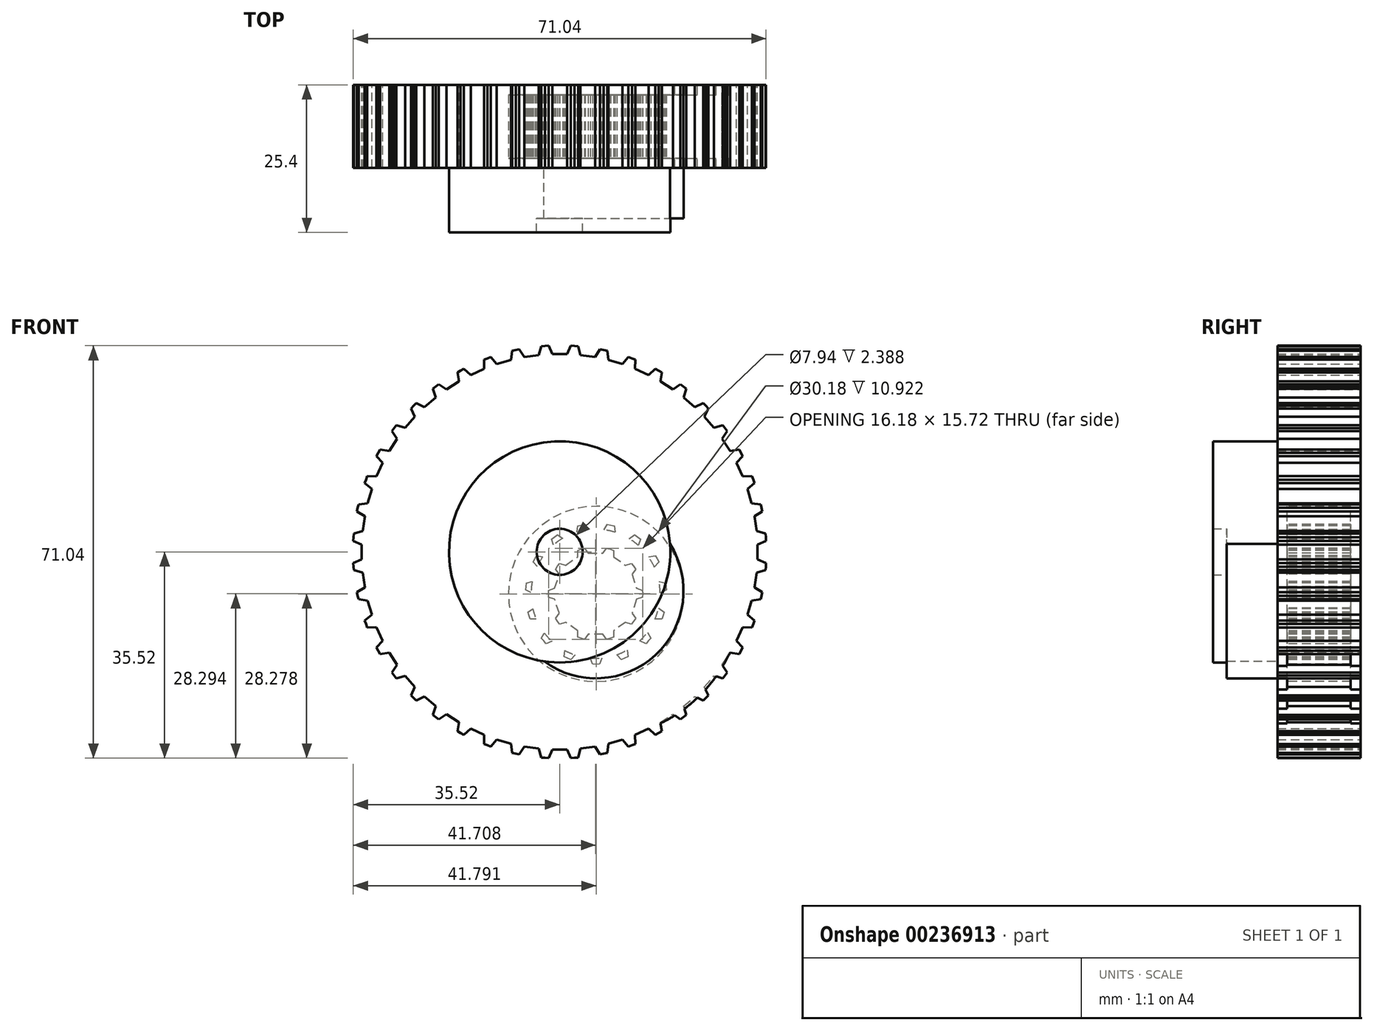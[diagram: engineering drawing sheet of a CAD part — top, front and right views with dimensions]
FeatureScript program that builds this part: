
annotation { "Feature Type Name" : "Feature", "Feature Type Description" : "" }
export const myFeature = defineFeature(function(context is Context, id is Id, definition is map)
    precondition{}
    {
        {
            var Q0;
            Q0=qCreatedBy(makeId("Front.planeOp"),FACE);
            var sketch = newSketch(context, id + "F0", { "sketchPlane" : qUnion([Q0])});
            skCircle(sketch, "E0", {"center": v(0, 0) * mm, "radius": 15.09 * mm});
            skCircle(sketch, "E1", {"center": v(0, 0) * mm, "radius": 22.64 * mm, "construction": true});
            skCircle(sketch, "E2", {"center": v(0, 0) * mm, "radius": 3.17 * mm});
            skCircle(sketch, "E3", {"center": v(0, 0) * mm, "radius": 25.4 * mm});
            skPoint(sketch, "E4", {"position": v(-2.54, 22.5) * mm});
            skPoint(sketch, "E5", {"position": v(2.54, 22.5) * mm});
            skPoint(sketch, "E6", {"position": v(-1.9, 22.56) * mm});
            skPoint(sketch, "E7", {"position": v(1.9, 22.56) * mm});
            skLineSegment(sketch, "E8", {"start": v(-2.54, 22.5) * mm, "end": v(-1.9, 22.56) * mm});
            skLineSegment(sketch, "E9", {"start": v(1.9, 22.56) * mm, "end": v(2.54, 22.5) * mm});
            skLineSegment(sketch, "E10", {"start": v(-1.9, 22.56) * mm, "end": v(-1.27, 21.24) * mm});
            skLineSegment(sketch, "E11", {"start": v(-1.27, 21.24) * mm, "end": v(1.27, 21.24) * mm});
            skLineSegment(sketch, "E12", {"start": v(1.27, 21.24) * mm, "end": v(1.9, 22.56) * mm});
            skLineSegment(sketch, "E13.1.0", {"start": v(-7.48, 21.37) * mm, "end": v(-6.88, 21.57) * mm});
            skLineSegment(sketch, "E13.1.1", {"start": v(-6.88, 21.57) * mm, "end": v(-5.96, 20.43) * mm});
            skLineSegment(sketch, "E13.1.2", {"start": v(-5.96, 20.43) * mm, "end": v(-3.49, 21) * mm});
            skLineSegment(sketch, "E13.1.3", {"start": v(-3.49, 21) * mm, "end": v(-3.16, 22.42) * mm});
            skLineSegment(sketch, "E13.1.4", {"start": v(-3.16, 22.42) * mm, "end": v(-2.53, 22.5) * mm});
            skLineSegment(sketch, "E13.2.0", {"start": v(-12.05, 19.17) * mm, "end": v(-11.5, 19.5) * mm});
            skLineSegment(sketch, "E13.2.1", {"start": v(-11.5, 19.5) * mm, "end": v(-10.36, 18.59) * mm});
            skLineSegment(sketch, "E13.2.2", {"start": v(-10.36, 18.59) * mm, "end": v(-8.07, 19.69) * mm});
            skLineSegment(sketch, "E13.2.3", {"start": v(-8.07, 19.69) * mm, "end": v(-8.07, 21.16) * mm});
            skLineSegment(sketch, "E13.2.4", {"start": v(-8.07, 21.16) * mm, "end": v(-7.47, 21.37) * mm});
            skLineSegment(sketch, "E13.3.0", {"start": v(-16.02, 16) * mm, "end": v(-15.56, 16.45) * mm});
            skLineSegment(sketch, "E13.3.1", {"start": v(-15.56, 16.45) * mm, "end": v(-14.24, 15.81) * mm});
            skLineSegment(sketch, "E13.3.2", {"start": v(-14.24, 15.81) * mm, "end": v(-12.25, 17.4) * mm});
            skLineSegment(sketch, "E13.3.3", {"start": v(-12.25, 17.4) * mm, "end": v(-12.58, 18.83) * mm});
            skLineSegment(sketch, "E13.3.4", {"start": v(-12.58, 18.83) * mm, "end": v(-12.04, 19.18) * mm});
            skLineSegment(sketch, "E13.4.0", {"start": v(-19.18, 12.04) * mm, "end": v(-18.83, 12.58) * mm});
            skLineSegment(sketch, "E13.4.1", {"start": v(-18.83, 12.58) * mm, "end": v(-17.4, 12.25) * mm});
            skLineSegment(sketch, "E13.4.2", {"start": v(-17.4, 12.25) * mm, "end": v(-15.81, 14.24) * mm});
            skLineSegment(sketch, "E13.4.3", {"start": v(-15.81, 14.24) * mm, "end": v(-16.45, 15.56) * mm});
            skLineSegment(sketch, "E13.4.4", {"start": v(-16.45, 15.56) * mm, "end": v(-16, 16.02) * mm});
            skLineSegment(sketch, "E13.5.0", {"start": v(-21.37, 7.47) * mm, "end": v(-21.16, 8.07) * mm});
            skLineSegment(sketch, "E13.5.1", {"start": v(-21.16, 8.07) * mm, "end": v(-19.69, 8.07) * mm});
            skLineSegment(sketch, "E13.5.2", {"start": v(-19.69, 8.07) * mm, "end": v(-18.59, 10.36) * mm});
            skLineSegment(sketch, "E13.5.3", {"start": v(-18.59, 10.36) * mm, "end": v(-19.5, 11.5) * mm});
            skLineSegment(sketch, "E13.5.4", {"start": v(-19.5, 11.5) * mm, "end": v(-19.17, 12.05) * mm});
            skLineSegment(sketch, "E13.6.0", {"start": v(-22.5, 2.53) * mm, "end": v(-22.42, 3.16) * mm});
            skLineSegment(sketch, "E13.6.1", {"start": v(-22.42, 3.16) * mm, "end": v(-21, 3.49) * mm});
            skLineSegment(sketch, "E13.6.2", {"start": v(-21, 3.49) * mm, "end": v(-20.43, 5.96) * mm});
            skLineSegment(sketch, "E13.6.3", {"start": v(-20.43, 5.96) * mm, "end": v(-21.57, 6.88) * mm});
            skLineSegment(sketch, "E13.6.4", {"start": v(-21.57, 6.88) * mm, "end": v(-21.37, 7.48) * mm});
            skLineSegment(sketch, "E13.7.0", {"start": v(-22.5, -2.54) * mm, "end": v(-22.56, -1.9) * mm});
            skLineSegment(sketch, "E13.7.1", {"start": v(-22.56, -1.9) * mm, "end": v(-21.24, -1.27) * mm});
            skLineSegment(sketch, "E13.7.2", {"start": v(-21.24, -1.27) * mm, "end": v(-21.24, 1.27) * mm});
            skLineSegment(sketch, "E13.7.3", {"start": v(-21.24, 1.27) * mm, "end": v(-22.56, 1.9) * mm});
            skLineSegment(sketch, "E13.7.4", {"start": v(-22.56, 1.9) * mm, "end": v(-22.5, 2.54) * mm});
            skLineSegment(sketch, "E13.8.0", {"start": v(-21.37, -7.48) * mm, "end": v(-21.57, -6.88) * mm});
            skLineSegment(sketch, "E13.8.1", {"start": v(-21.57, -6.88) * mm, "end": v(-20.43, -5.96) * mm});
            skLineSegment(sketch, "E13.8.2", {"start": v(-20.43, -5.96) * mm, "end": v(-21, -3.49) * mm});
            skLineSegment(sketch, "E13.8.3", {"start": v(-21, -3.49) * mm, "end": v(-22.42, -3.16) * mm});
            skLineSegment(sketch, "E13.8.4", {"start": v(-22.42, -3.16) * mm, "end": v(-22.5, -2.53) * mm});
            skLineSegment(sketch, "E13.9.0", {"start": v(-19.17, -12.05) * mm, "end": v(-19.5, -11.5) * mm});
            skLineSegment(sketch, "E13.9.1", {"start": v(-19.5, -11.5) * mm, "end": v(-18.59, -10.36) * mm});
            skLineSegment(sketch, "E13.9.2", {"start": v(-18.59, -10.36) * mm, "end": v(-19.69, -8.07) * mm});
            skLineSegment(sketch, "E13.9.3", {"start": v(-19.69, -8.07) * mm, "end": v(-21.16, -8.07) * mm});
            skLineSegment(sketch, "E13.9.4", {"start": v(-21.16, -8.07) * mm, "end": v(-21.37, -7.47) * mm});
            skLineSegment(sketch, "E13.10.0", {"start": v(-16, -16.02) * mm, "end": v(-16.45, -15.56) * mm});
            skLineSegment(sketch, "E13.10.1", {"start": v(-16.45, -15.56) * mm, "end": v(-15.81, -14.24) * mm});
            skLineSegment(sketch, "E13.10.2", {"start": v(-15.81, -14.24) * mm, "end": v(-17.4, -12.25) * mm});
            skLineSegment(sketch, "E13.10.3", {"start": v(-17.4, -12.25) * mm, "end": v(-18.83, -12.58) * mm});
            skLineSegment(sketch, "E13.10.4", {"start": v(-18.83, -12.58) * mm, "end": v(-19.18, -12.04) * mm});
            skLineSegment(sketch, "E13.11.0", {"start": v(-12.04, -19.18) * mm, "end": v(-12.58, -18.83) * mm});
            skLineSegment(sketch, "E13.11.1", {"start": v(-12.58, -18.83) * mm, "end": v(-12.25, -17.4) * mm});
            skLineSegment(sketch, "E13.11.2", {"start": v(-12.25, -17.4) * mm, "end": v(-14.24, -15.81) * mm});
            skLineSegment(sketch, "E13.11.3", {"start": v(-14.24, -15.81) * mm, "end": v(-15.56, -16.45) * mm});
            skLineSegment(sketch, "E13.11.4", {"start": v(-15.56, -16.45) * mm, "end": v(-16.02, -16) * mm});
            skLineSegment(sketch, "E13.12.0", {"start": v(-7.47, -21.37) * mm, "end": v(-8.07, -21.16) * mm});
            skLineSegment(sketch, "E13.12.1", {"start": v(-8.07, -21.16) * mm, "end": v(-8.07, -19.69) * mm});
            skLineSegment(sketch, "E13.12.2", {"start": v(-8.07, -19.69) * mm, "end": v(-10.36, -18.59) * mm});
            skLineSegment(sketch, "E13.12.3", {"start": v(-10.36, -18.59) * mm, "end": v(-11.5, -19.5) * mm});
            skLineSegment(sketch, "E13.12.4", {"start": v(-11.5, -19.5) * mm, "end": v(-12.05, -19.17) * mm});
            skLineSegment(sketch, "E13.13.0", {"start": v(-2.53, -22.5) * mm, "end": v(-3.16, -22.42) * mm});
            skLineSegment(sketch, "E13.13.1", {"start": v(-3.16, -22.42) * mm, "end": v(-3.49, -21) * mm});
            skLineSegment(sketch, "E13.13.2", {"start": v(-3.49, -21) * mm, "end": v(-5.96, -20.43) * mm});
            skLineSegment(sketch, "E13.13.3", {"start": v(-5.96, -20.43) * mm, "end": v(-6.88, -21.57) * mm});
            skLineSegment(sketch, "E13.13.4", {"start": v(-6.88, -21.57) * mm, "end": v(-7.48, -21.37) * mm});
            skLineSegment(sketch, "E13.14.0", {"start": v(2.54, -22.5) * mm, "end": v(1.9, -22.56) * mm});
            skLineSegment(sketch, "E13.14.1", {"start": v(1.9, -22.56) * mm, "end": v(1.27, -21.24) * mm});
            skLineSegment(sketch, "E13.14.2", {"start": v(1.27, -21.24) * mm, "end": v(-1.27, -21.24) * mm});
            skLineSegment(sketch, "E13.14.3", {"start": v(-1.27, -21.24) * mm, "end": v(-1.9, -22.56) * mm});
            skLineSegment(sketch, "E13.14.4", {"start": v(-1.9, -22.56) * mm, "end": v(-2.54, -22.5) * mm});
            skLineSegment(sketch, "E13.15.0", {"start": v(7.48, -21.37) * mm, "end": v(6.88, -21.57) * mm});
            skLineSegment(sketch, "E13.15.1", {"start": v(6.88, -21.57) * mm, "end": v(5.96, -20.43) * mm});
            skLineSegment(sketch, "E13.15.2", {"start": v(5.96, -20.43) * mm, "end": v(3.49, -21) * mm});
            skLineSegment(sketch, "E13.15.3", {"start": v(3.49, -21) * mm, "end": v(3.16, -22.42) * mm});
            skLineSegment(sketch, "E13.15.4", {"start": v(3.16, -22.42) * mm, "end": v(2.53, -22.5) * mm});
            skLineSegment(sketch, "E13.16.0", {"start": v(12.05, -19.17) * mm, "end": v(11.5, -19.5) * mm});
            skLineSegment(sketch, "E13.16.1", {"start": v(11.5, -19.5) * mm, "end": v(10.36, -18.59) * mm});
            skLineSegment(sketch, "E13.16.2", {"start": v(10.36, -18.59) * mm, "end": v(8.07, -19.69) * mm});
            skLineSegment(sketch, "E13.16.3", {"start": v(8.07, -19.69) * mm, "end": v(8.07, -21.16) * mm});
            skLineSegment(sketch, "E13.16.4", {"start": v(8.07, -21.16) * mm, "end": v(7.47, -21.37) * mm});
            skLineSegment(sketch, "E13.17.0", {"start": v(16.02, -16) * mm, "end": v(15.56, -16.45) * mm});
            skLineSegment(sketch, "E13.17.1", {"start": v(15.56, -16.45) * mm, "end": v(14.24, -15.81) * mm});
            skLineSegment(sketch, "E13.17.2", {"start": v(14.24, -15.81) * mm, "end": v(12.25, -17.4) * mm});
            skLineSegment(sketch, "E13.17.3", {"start": v(12.25, -17.4) * mm, "end": v(12.58, -18.83) * mm});
            skLineSegment(sketch, "E13.17.4", {"start": v(12.58, -18.83) * mm, "end": v(12.04, -19.18) * mm});
            skLineSegment(sketch, "E13.18.0", {"start": v(19.18, -12.04) * mm, "end": v(18.83, -12.58) * mm});
            skLineSegment(sketch, "E13.18.1", {"start": v(18.83, -12.58) * mm, "end": v(17.4, -12.25) * mm});
            skLineSegment(sketch, "E13.18.2", {"start": v(17.4, -12.25) * mm, "end": v(15.81, -14.24) * mm});
            skLineSegment(sketch, "E13.18.3", {"start": v(15.81, -14.24) * mm, "end": v(16.45, -15.56) * mm});
            skLineSegment(sketch, "E13.18.4", {"start": v(16.45, -15.56) * mm, "end": v(16, -16.02) * mm});
            skLineSegment(sketch, "E13.19.0", {"start": v(21.37, -7.47) * mm, "end": v(21.16, -8.07) * mm});
            skLineSegment(sketch, "E13.19.1", {"start": v(21.16, -8.07) * mm, "end": v(19.69, -8.07) * mm});
            skLineSegment(sketch, "E13.19.2", {"start": v(19.69, -8.07) * mm, "end": v(18.59, -10.36) * mm});
            skLineSegment(sketch, "E13.19.3", {"start": v(18.59, -10.36) * mm, "end": v(19.5, -11.5) * mm});
            skLineSegment(sketch, "E13.19.4", {"start": v(19.5, -11.5) * mm, "end": v(19.17, -12.05) * mm});
            skLineSegment(sketch, "E13.20.0", {"start": v(22.5, -2.53) * mm, "end": v(22.42, -3.16) * mm});
            skLineSegment(sketch, "E13.20.1", {"start": v(22.42, -3.16) * mm, "end": v(21, -3.49) * mm});
            skLineSegment(sketch, "E13.20.2", {"start": v(21, -3.49) * mm, "end": v(20.43, -5.96) * mm});
            skLineSegment(sketch, "E13.20.3", {"start": v(20.43, -5.96) * mm, "end": v(21.57, -6.88) * mm});
            skLineSegment(sketch, "E13.20.4", {"start": v(21.57, -6.88) * mm, "end": v(21.37, -7.48) * mm});
            skLineSegment(sketch, "E13.21.0", {"start": v(22.5, 2.54) * mm, "end": v(22.56, 1.9) * mm});
            skLineSegment(sketch, "E13.21.1", {"start": v(22.56, 1.9) * mm, "end": v(21.24, 1.27) * mm});
            skLineSegment(sketch, "E13.21.2", {"start": v(21.24, 1.27) * mm, "end": v(21.24, -1.27) * mm});
            skLineSegment(sketch, "E13.21.3", {"start": v(21.24, -1.27) * mm, "end": v(22.56, -1.9) * mm});
            skLineSegment(sketch, "E13.21.4", {"start": v(22.56, -1.9) * mm, "end": v(22.5, -2.54) * mm});
            skLineSegment(sketch, "E13.22.0", {"start": v(21.37, 7.48) * mm, "end": v(21.57, 6.88) * mm});
            skLineSegment(sketch, "E13.22.1", {"start": v(21.57, 6.88) * mm, "end": v(20.43, 5.96) * mm});
            skLineSegment(sketch, "E13.22.2", {"start": v(20.43, 5.96) * mm, "end": v(21, 3.49) * mm});
            skLineSegment(sketch, "E13.22.3", {"start": v(21, 3.49) * mm, "end": v(22.42, 3.16) * mm});
            skLineSegment(sketch, "E13.22.4", {"start": v(22.42, 3.16) * mm, "end": v(22.5, 2.53) * mm});
            skLineSegment(sketch, "E13.23.0", {"start": v(19.17, 12.05) * mm, "end": v(19.5, 11.5) * mm});
            skLineSegment(sketch, "E13.23.1", {"start": v(19.5, 11.5) * mm, "end": v(18.59, 10.36) * mm});
            skLineSegment(sketch, "E13.23.2", {"start": v(18.59, 10.36) * mm, "end": v(19.69, 8.07) * mm});
            skLineSegment(sketch, "E13.23.3", {"start": v(19.69, 8.07) * mm, "end": v(21.16, 8.07) * mm});
            skLineSegment(sketch, "E13.23.4", {"start": v(21.16, 8.07) * mm, "end": v(21.37, 7.47) * mm});
            skLineSegment(sketch, "E13.24.0", {"start": v(16, 16.02) * mm, "end": v(16.45, 15.56) * mm});
            skLineSegment(sketch, "E13.24.1", {"start": v(16.45, 15.56) * mm, "end": v(15.81, 14.24) * mm});
            skLineSegment(sketch, "E13.24.2", {"start": v(15.81, 14.24) * mm, "end": v(17.4, 12.25) * mm});
            skLineSegment(sketch, "E13.24.3", {"start": v(17.4, 12.25) * mm, "end": v(18.83, 12.58) * mm});
            skLineSegment(sketch, "E13.24.4", {"start": v(18.83, 12.58) * mm, "end": v(19.18, 12.04) * mm});
            skLineSegment(sketch, "E13.25.0", {"start": v(12.04, 19.18) * mm, "end": v(12.58, 18.83) * mm});
            skLineSegment(sketch, "E13.25.1", {"start": v(12.58, 18.83) * mm, "end": v(12.25, 17.4) * mm});
            skLineSegment(sketch, "E13.25.2", {"start": v(12.25, 17.4) * mm, "end": v(14.24, 15.81) * mm});
            skLineSegment(sketch, "E13.25.3", {"start": v(14.24, 15.81) * mm, "end": v(15.56, 16.45) * mm});
            skLineSegment(sketch, "E13.25.4", {"start": v(15.56, 16.45) * mm, "end": v(16.02, 16) * mm});
            skLineSegment(sketch, "E13.26.0", {"start": v(7.47, 21.37) * mm, "end": v(8.07, 21.16) * mm});
            skLineSegment(sketch, "E13.26.1", {"start": v(8.07, 21.16) * mm, "end": v(8.07, 19.69) * mm});
            skLineSegment(sketch, "E13.26.2", {"start": v(8.07, 19.69) * mm, "end": v(10.36, 18.59) * mm});
            skLineSegment(sketch, "E13.26.3", {"start": v(10.36, 18.59) * mm, "end": v(11.5, 19.5) * mm});
            skLineSegment(sketch, "E13.26.4", {"start": v(11.5, 19.5) * mm, "end": v(12.05, 19.17) * mm});
            skLineSegment(sketch, "E13.27.0", {"start": v(2.53, 22.5) * mm, "end": v(3.16, 22.42) * mm});
            skLineSegment(sketch, "E13.27.1", {"start": v(3.16, 22.42) * mm, "end": v(3.49, 21) * mm});
            skLineSegment(sketch, "E13.27.2", {"start": v(3.49, 21) * mm, "end": v(5.96, 20.43) * mm});
            skLineSegment(sketch, "E13.27.3", {"start": v(5.96, 20.43) * mm, "end": v(6.88, 21.57) * mm});
            skLineSegment(sketch, "E13.27.4", {"start": v(6.88, 21.57) * mm, "end": v(7.48, 21.37) * mm});
            skSolve(sketch);
        }
        {
            var Q0;
            Q0=makeQuery(id+"F0.imprint","IMPRINT",FACE,{"disambiguationData":[TD([[makeQuery(id+"F0.imprint","IMPRINT",EDGE,{"derivedFrom":sQuery(id+"F0.wireOp",EDGE,"E3")}),1.0]])]});
            var Q1;
            Q1=makeQuery(id+"F0.imprint","IMPRINT",FACE,{"disambiguationData":[TD([[makeQuery(id+"F0.imprint","IMPRINT",EDGE,{"derivedFrom":sQuery(id+"F0.wireOp",EDGE,"E0")}),-1.0]])]});
            var Q2;
            Q2=makeQuery(id+"F0.imprint","IMPRINT",FACE,{"disambiguationData":[TD([[makeQuery(id+"F0.imprint","IMPRINT",EDGE,{"derivedFrom":sQuery(id+"F0.wireOp",EDGE,"E0")}),1.0]])]});
            extrude(context, id + "F1", {"entities" : qUnion([Q0, Q1, Q2]), "endBound" : BoundingType.SYMMETRIC, "depth" : 14.3 * mm});
        }
        {
            var Q0;
            Q0=makeQuery(id+"F0.imprint","IMPRINT",FACE,{"disambiguationData":[TD([[makeQuery(id+"F0.imprint","IMPRINT",EDGE,{"derivedFrom":sQuery(id+"F0.wireOp",EDGE,"E3")}),1.0]])]});
            extrude(context, id + "F2", {"entities" : qUnion([Q0]), "operationType" : NewBodyOperationType.REMOVE, "endBound" : BoundingType.SYMMETRIC, "oppositeDirection" : true, "depth" : 10.92 * mm});
        }
        {
            var Q0;
            Q0=makeQuery(id+"F0.imprint","IMPRINT",FACE,{"disambiguationData":[TD([[makeQuery(id+"F0.imprint","IMPRINT",EDGE,{"derivedFrom":sQuery(id+"F0.wireOp",EDGE,"E0")}),1.0]])]});
            var Q1;
            Q1=makeQuery(id+"F1.opExtrude","SWEPT_BODY",BODY,{"disambiguationData":[OSD([sQuery(id+"F0.wireOp",EDGE,"E2"),sQuery(id+"F0.wireOp",EDGE,"E3")])]});
            extrude(context, id + "F3", {"entities" : qUnion([Q0]), "operationType" : NewBodyOperationType.ADD, "endBoundEntityBody" : qUnion([Q1]), "depth" : 15.86 * mm});
        }
        {
            var Q0;
            Q0=qCreatedBy(makeId("Front.planeOp"),FACE);
            var sketch = newSketch(context, id + "F4", { "sketchPlane" : qUnion([Q0])});
            skCircle(sketch, "E14", {"center": v(3.09, 5.3) * mm, "radius": 7.15 * mm});
            skCircle(sketch, "E15", {"center": v(3.09, 5.3) * mm, "radius": 11.32 * mm, "construction": true});
            skCircle(sketch, "E16", {"center": v(3.09, 5.3) * mm, "radius": 3.17 * mm});
            skCircle(sketch, "E17", {"center": v(3.09, 5.3) * mm, "radius": 13.9 * mm});
            skPoint(sketch, "E18", {"position": v(0.55, 16.33) * mm});
            skPoint(sketch, "E19", {"position": v(5.63, 16.33) * mm});
            skPoint(sketch, "E20", {"position": v(1.18, 16.46) * mm});
            skPoint(sketch, "E21", {"position": v(5, 16.46) * mm});
            skLineSegment(sketch, "E22", {"start": v(0.55, 16.33) * mm, "end": v(1.18, 16.46) * mm});
            skLineSegment(sketch, "E23", {"start": v(5, 16.46) * mm, "end": v(5.63, 16.33) * mm});
            skLineSegment(sketch, "E24", {"start": v(1.18, 16.46) * mm, "end": v(1.82, 15.42) * mm});
            skLineSegment(sketch, "E25", {"start": v(1.82, 15.42) * mm, "end": v(4.36, 15.42) * mm});
            skLineSegment(sketch, "E26", {"start": v(4.36, 15.42) * mm, "end": v(5, 16.46) * mm});
            skLineSegment(sketch, "E27.1.0", {"start": v(-3.99, 14.14) * mm, "end": v(-3.47, 14.53) * mm});
            skLineSegment(sketch, "E27.1.1", {"start": v(-3.47, 14.53) * mm, "end": v(-2.44, 13.87) * mm});
            skLineSegment(sketch, "E27.1.2", {"start": v(-2.44, 13.87) * mm, "end": v(-0.16, 14.97) * mm});
            skLineSegment(sketch, "E27.1.3", {"start": v(-0.16, 14.97) * mm, "end": v(-0.04, 16.18) * mm});
            skLineSegment(sketch, "E27.1.4", {"start": v(-0.04, 16.18) * mm, "end": v(0.6, 16.34) * mm});
            skLineSegment(sketch, "E27.2.0", {"start": v(-7.12, 10.2) * mm, "end": v(-6.82, 10.77) * mm});
            skLineSegment(sketch, "E27.2.1", {"start": v(-6.82, 10.77) * mm, "end": v(-5.6, 10.62) * mm});
            skLineSegment(sketch, "E27.2.2", {"start": v(-5.6, 10.62) * mm, "end": v(-4.03, 12.6) * mm});
            skLineSegment(sketch, "E27.2.3", {"start": v(-4.03, 12.6) * mm, "end": v(-4.45, 13.75) * mm});
            skLineSegment(sketch, "E27.2.4", {"start": v(-4.45, 13.75) * mm, "end": v(-3.95, 14.17) * mm});
            skLineSegment(sketch, "E27.3.0", {"start": v(-8.23, 5.28) * mm, "end": v(-8.21, 5.93) * mm});
            skLineSegment(sketch, "E27.3.1", {"start": v(-8.21, 5.93) * mm, "end": v(-7.05, 6.32) * mm});
            skLineSegment(sketch, "E27.3.2", {"start": v(-7.05, 6.32) * mm, "end": v(-6.49, 8.8) * mm});
            skLineSegment(sketch, "E27.3.3", {"start": v(-6.49, 8.8) * mm, "end": v(-7.36, 9.65) * mm});
            skLineSegment(sketch, "E27.3.4", {"start": v(-7.36, 9.65) * mm, "end": v(-7.1, 10.24) * mm});
            skLineSegment(sketch, "E27.4.0", {"start": v(-7.1, 0.38) * mm, "end": v(-7.36, 0.97) * mm});
            skLineSegment(sketch, "E27.4.1", {"start": v(-7.36, 0.97) * mm, "end": v(-6.49, 1.82) * mm});
            skLineSegment(sketch, "E27.4.2", {"start": v(-6.49, 1.82) * mm, "end": v(-7.05, 4.3) * mm});
            skLineSegment(sketch, "E27.4.3", {"start": v(-7.05, 4.3) * mm, "end": v(-8.21, 4.68) * mm});
            skLineSegment(sketch, "E27.4.4", {"start": v(-8.21, 4.68) * mm, "end": v(-8.23, 5.33) * mm});
            skLineSegment(sketch, "E27.5.0", {"start": v(-3.95, -3.55) * mm, "end": v(-4.45, -3.14) * mm});
            skLineSegment(sketch, "E27.5.1", {"start": v(-4.45, -3.14) * mm, "end": v(-4.03, -1.99) * mm});
            skLineSegment(sketch, "E27.5.2", {"start": v(-4.03, -1.99) * mm, "end": v(-5.6, 0) * mm});
            skLineSegment(sketch, "E27.5.3", {"start": v(-5.6, 0) * mm, "end": v(-6.82, -0.16) * mm});
            skLineSegment(sketch, "E27.5.4", {"start": v(-6.82, -0.16) * mm, "end": v(-7.12, 0.42) * mm});
            skLineSegment(sketch, "E27.6.0", {"start": v(0.6, -5.73) * mm, "end": v(-0.04, -5.57) * mm});
            skLineSegment(sketch, "E27.6.1", {"start": v(-0.04, -5.57) * mm, "end": v(-0.16, -4.35) * mm});
            skLineSegment(sketch, "E27.6.2", {"start": v(-0.16, -4.35) * mm, "end": v(-2.44, -3.25) * mm});
            skLineSegment(sketch, "E27.6.3", {"start": v(-2.44, -3.25) * mm, "end": v(-3.47, -3.92) * mm});
            skLineSegment(sketch, "E27.6.4", {"start": v(-3.47, -3.92) * mm, "end": v(-3.99, -3.53) * mm});
            skLineSegment(sketch, "E27.7.0", {"start": v(5.63, -5.72) * mm, "end": v(5, -5.85) * mm});
            skLineSegment(sketch, "E27.7.1", {"start": v(5, -5.85) * mm, "end": v(4.36, -4.8) * mm});
            skLineSegment(sketch, "E27.7.2", {"start": v(4.36, -4.8) * mm, "end": v(1.82, -4.8) * mm});
            skLineSegment(sketch, "E27.7.3", {"start": v(1.82, -4.8) * mm, "end": v(1.18, -5.85) * mm});
            skLineSegment(sketch, "E27.7.4", {"start": v(1.18, -5.85) * mm, "end": v(0.55, -5.72) * mm});
            skLineSegment(sketch, "E27.8.0", {"start": v(10.16, -3.53) * mm, "end": v(9.64, -3.92) * mm});
            skLineSegment(sketch, "E27.8.1", {"start": v(9.64, -3.92) * mm, "end": v(8.62, -3.25) * mm});
            skLineSegment(sketch, "E27.8.2", {"start": v(8.62, -3.25) * mm, "end": v(6.33, -4.35) * mm});
            skLineSegment(sketch, "E27.8.3", {"start": v(6.33, -4.35) * mm, "end": v(6.21, -5.57) * mm});
            skLineSegment(sketch, "E27.8.4", {"start": v(6.21, -5.57) * mm, "end": v(5.58, -5.73) * mm});
            skLineSegment(sketch, "E27.9.0", {"start": v(13.3, 0.42) * mm, "end": v(13, -0.16) * mm});
            skLineSegment(sketch, "E27.9.1", {"start": v(13, -0.16) * mm, "end": v(11.78, 0) * mm});
            skLineSegment(sketch, "E27.9.2", {"start": v(11.78, 0) * mm, "end": v(10.2, -1.99) * mm});
            skLineSegment(sketch, "E27.9.3", {"start": v(10.2, -1.99) * mm, "end": v(10.62, -3.14) * mm});
            skLineSegment(sketch, "E27.9.4", {"start": v(10.62, -3.14) * mm, "end": v(10.12, -3.55) * mm});
            skLineSegment(sketch, "E27.10.0", {"start": v(14.4, 5.33) * mm, "end": v(14.39, 4.68) * mm});
            skLineSegment(sketch, "E27.10.1", {"start": v(14.39, 4.68) * mm, "end": v(13.23, 4.3) * mm});
            skLineSegment(sketch, "E27.10.2", {"start": v(13.23, 4.3) * mm, "end": v(12.66, 1.82) * mm});
            skLineSegment(sketch, "E27.10.3", {"start": v(12.66, 1.82) * mm, "end": v(13.54, 0.97) * mm});
            skLineSegment(sketch, "E27.10.4", {"start": v(13.54, 0.97) * mm, "end": v(13.27, 0.38) * mm});
            skLineSegment(sketch, "E27.11.0", {"start": v(13.27, 10.24) * mm, "end": v(13.54, 9.65) * mm});
            skLineSegment(sketch, "E27.11.1", {"start": v(13.54, 9.65) * mm, "end": v(12.66, 8.8) * mm});
            skLineSegment(sketch, "E27.11.2", {"start": v(12.66, 8.8) * mm, "end": v(13.23, 6.32) * mm});
            skLineSegment(sketch, "E27.11.3", {"start": v(13.23, 6.32) * mm, "end": v(14.39, 5.93) * mm});
            skLineSegment(sketch, "E27.11.4", {"start": v(14.39, 5.93) * mm, "end": v(14.4, 5.28) * mm});
            skLineSegment(sketch, "E27.12.0", {"start": v(10.12, 14.17) * mm, "end": v(10.62, 13.75) * mm});
            skLineSegment(sketch, "E27.12.1", {"start": v(10.62, 13.75) * mm, "end": v(10.2, 12.6) * mm});
            skLineSegment(sketch, "E27.12.2", {"start": v(10.2, 12.6) * mm, "end": v(11.78, 10.62) * mm});
            skLineSegment(sketch, "E27.12.3", {"start": v(11.78, 10.62) * mm, "end": v(13, 10.77) * mm});
            skLineSegment(sketch, "E27.12.4", {"start": v(13, 10.77) * mm, "end": v(13.3, 10.2) * mm});
            skLineSegment(sketch, "E27.13.0", {"start": v(5.58, 16.34) * mm, "end": v(6.21, 16.18) * mm});
            skLineSegment(sketch, "E27.13.1", {"start": v(6.21, 16.18) * mm, "end": v(6.33, 14.97) * mm});
            skLineSegment(sketch, "E27.13.2", {"start": v(6.33, 14.97) * mm, "end": v(8.62, 13.87) * mm});
            skLineSegment(sketch, "E27.13.3", {"start": v(8.62, 13.87) * mm, "end": v(9.64, 14.53) * mm});
            skLineSegment(sketch, "E27.13.4", {"start": v(9.64, 14.53) * mm, "end": v(10.16, 14.14) * mm});
            skSolve(sketch);
        }
        {
            var Q0;
            Q0=makeQuery(id+"F4.imprint","IMPRINT",FACE,{"disambiguationData":[TD([[makeQuery(id+"F4.imprint","IMPRINT",EDGE,{"derivedFrom":sQuery(id+"F4.wireOp",EDGE,"E17")}),1.0]])]});
            var Q1;
            Q1=makeQuery(id+"F4.imprint","IMPRINT",FACE,{"disambiguationData":[TD([[makeQuery(id+"F4.imprint","IMPRINT",EDGE,{"derivedFrom":sQuery(id+"F4.wireOp",EDGE,"E14")}),-1.0]])]});
            var Q2;
            Q2=makeQuery(id+"F4.imprint","IMPRINT",FACE,{"disambiguationData":[TD([[makeQuery(id+"F4.imprint","IMPRINT",EDGE,{"derivedFrom":sQuery(id+"F4.wireOp",EDGE,"E14")}),1.0]])]});
            extrude(context, id + "F5", {"entities" : qUnion([Q0, Q1, Q2]), "endBound" : BoundingType.SYMMETRIC, "depth" : 14.3 * mm});
        }
        {
            var Q0;
            Q0=makeQuery(id+"F4.imprint","IMPRINT",FACE,{"disambiguationData":[TD([[makeQuery(id+"F4.imprint","IMPRINT",EDGE,{"derivedFrom":sQuery(id+"F4.wireOp",EDGE,"E17")}),1.0]])]});
            extrude(context, id + "F6", {"entities" : qUnion([Q0]), "operationType" : NewBodyOperationType.REMOVE, "endBound" : BoundingType.SYMMETRIC, "oppositeDirection" : true, "depth" : 10.92 * mm});
        }
        {
            var Q0;
            Q0=makeQuery(id+"F4.imprint","IMPRINT",FACE,{"disambiguationData":[TD([[makeQuery(id+"F4.imprint","IMPRINT",EDGE,{"derivedFrom":sQuery(id+"F4.wireOp",EDGE,"E14")}),1.0]])]});
            extrude(context, id + "F7", {"entities" : qUnion([Q0]), "operationType" : NewBodyOperationType.ADD, "depth" : 13.47 * mm});
        }
        {
            var Q0;
            Q0=qCreatedBy(makeId("Front.planeOp"),FACE);
            var sketch = newSketch(context, id + "F8", { "sketchPlane" : qUnion([Q0])});
            skCircle(sketch, "E28", {"center": v(-0.25, -0.6) * mm, "radius": 10.31 * mm});
            skCircle(sketch, "E29", {"center": v(-0.25, -0.6) * mm, "radius": 14.55 * mm, "construction": true});
            skCircle(sketch, "E30", {"center": v(-0.25, -0.6) * mm, "radius": 3.17 * mm});
            skCircle(sketch, "E31", {"center": v(-0.25, -0.6) * mm, "radius": 17.46 * mm});
            skPoint(sketch, "E32", {"position": v(-2.79, 13.72) * mm});
            skPoint(sketch, "E33", {"position": v(2.3, 13.72) * mm});
            skPoint(sketch, "E34", {"position": v(-2.15, 13.82) * mm});
            skPoint(sketch, "E35", {"position": v(1.66, 13.82) * mm});
            skLineSegment(sketch, "E36", {"start": v(-2.79, 13.72) * mm, "end": v(-2.15, 13.82) * mm});
            skLineSegment(sketch, "E37", {"start": v(1.66, 13.82) * mm, "end": v(2.3, 13.72) * mm});
            skLineSegment(sketch, "E38", {"start": v(-2.15, 13.82) * mm, "end": v(-1.52, 12.66) * mm});
            skLineSegment(sketch, "E39", {"start": v(-1.52, 12.66) * mm, "end": v(1.02, 12.66) * mm});
            skLineSegment(sketch, "E40", {"start": v(1.02, 12.66) * mm, "end": v(1.66, 13.82) * mm});
            skLineSegment(sketch, "E41.1.0", {"start": v(-7.53, 11.99) * mm, "end": v(-6.97, 12.3) * mm});
            skLineSegment(sketch, "E41.1.1", {"start": v(-6.97, 12.3) * mm, "end": v(-5.98, 11.43) * mm});
            skLineSegment(sketch, "E41.1.2", {"start": v(-5.98, 11.43) * mm, "end": v(-3.6, 12.3) * mm});
            skLineSegment(sketch, "E41.1.3", {"start": v(-3.6, 12.3) * mm, "end": v(-3.4, 13.6) * mm});
            skLineSegment(sketch, "E41.1.4", {"start": v(-3.4, 13.6) * mm, "end": v(-2.76, 13.73) * mm});
            skLineSegment(sketch, "E41.2.0", {"start": v(-11.4, 8.74) * mm, "end": v(-10.98, 9.22) * mm});
            skLineSegment(sketch, "E41.2.1", {"start": v(-10.98, 9.22) * mm, "end": v(-9.75, 8.74) * mm});
            skLineSegment(sketch, "E41.2.2", {"start": v(-9.75, 8.74) * mm, "end": v(-7.8, 10.38) * mm});
            skLineSegment(sketch, "E41.2.3", {"start": v(-7.8, 10.38) * mm, "end": v(-8.06, 11.67) * mm});
            skLineSegment(sketch, "E41.2.4", {"start": v(-8.06, 11.67) * mm, "end": v(-7.51, 12) * mm});
            skLineSegment(sketch, "E41.3.0", {"start": v(-13.93, 4.36) * mm, "end": v(-13.7, 4.96) * mm});
            skLineSegment(sketch, "E41.3.1", {"start": v(-13.7, 4.96) * mm, "end": v(-12.38, 4.93) * mm});
            skLineSegment(sketch, "E41.3.2", {"start": v(-12.38, 4.93) * mm, "end": v(-11.1, 7.13) * mm});
            skLineSegment(sketch, "E41.3.3", {"start": v(-11.1, 7.13) * mm, "end": v(-11.79, 8.26) * mm});
            skLineSegment(sketch, "E41.3.4", {"start": v(-11.79, 8.26) * mm, "end": v(-11.39, 8.76) * mm});
            skLineSegment(sketch, "E41.4.0", {"start": v(-14.8, -0.62) * mm, "end": v(-14.79, 0.02) * mm});
            skLineSegment(sketch, "E41.4.1", {"start": v(-14.79, 0.02) * mm, "end": v(-13.54, 0.45) * mm});
            skLineSegment(sketch, "E41.4.2", {"start": v(-13.54, 0.45) * mm, "end": v(-13.1, 2.95) * mm});
            skLineSegment(sketch, "E41.4.3", {"start": v(-13.1, 2.95) * mm, "end": v(-14.13, 3.77) * mm});
            skLineSegment(sketch, "E41.4.4", {"start": v(-14.13, 3.77) * mm, "end": v(-13.92, 4.38) * mm});
            skLineSegment(sketch, "E41.5.0", {"start": v(-13.92, -5.6) * mm, "end": v(-14.13, -5) * mm});
            skLineSegment(sketch, "E41.5.1", {"start": v(-14.13, -5) * mm, "end": v(-13.1, -4.16) * mm});
            skLineSegment(sketch, "E41.5.2", {"start": v(-13.1, -4.16) * mm, "end": v(-13.54, -1.66) * mm});
            skLineSegment(sketch, "E41.5.3", {"start": v(-13.54, -1.66) * mm, "end": v(-14.79, -1.24) * mm});
            skLineSegment(sketch, "E41.5.4", {"start": v(-14.79, -1.24) * mm, "end": v(-14.8, -0.6) * mm});
            skLineSegment(sketch, "E41.6.0", {"start": v(-11.39, -9.97) * mm, "end": v(-11.79, -9.47) * mm});
            skLineSegment(sketch, "E41.6.1", {"start": v(-11.79, -9.47) * mm, "end": v(-11.1, -8.35) * mm});
            skLineSegment(sketch, "E41.6.2", {"start": v(-11.1, -8.35) * mm, "end": v(-12.38, -6.15) * mm});
            skLineSegment(sketch, "E41.6.3", {"start": v(-12.38, -6.15) * mm, "end": v(-13.7, -6.17) * mm});
            skLineSegment(sketch, "E41.6.4", {"start": v(-13.7, -6.17) * mm, "end": v(-13.93, -5.57) * mm});
            skLineSegment(sketch, "E41.7.0", {"start": v(-7.51, -13.22) * mm, "end": v(-8.06, -12.89) * mm});
            skLineSegment(sketch, "E41.7.1", {"start": v(-8.06, -12.89) * mm, "end": v(-7.8, -11.6) * mm});
            skLineSegment(sketch, "E41.7.2", {"start": v(-7.8, -11.6) * mm, "end": v(-9.75, -9.96) * mm});
            skLineSegment(sketch, "E41.7.3", {"start": v(-9.75, -9.96) * mm, "end": v(-10.98, -10.44) * mm});
            skLineSegment(sketch, "E41.7.4", {"start": v(-10.98, -10.44) * mm, "end": v(-11.4, -9.95) * mm});
            skLineSegment(sketch, "E41.8.0", {"start": v(-2.76, -14.94) * mm, "end": v(-3.4, -14.82) * mm});
            skLineSegment(sketch, "E41.8.1", {"start": v(-3.4, -14.82) * mm, "end": v(-3.6, -13.52) * mm});
            skLineSegment(sketch, "E41.8.2", {"start": v(-3.6, -13.52) * mm, "end": v(-5.98, -12.65) * mm});
            skLineSegment(sketch, "E41.8.3", {"start": v(-5.98, -12.65) * mm, "end": v(-6.97, -13.52) * mm});
            skLineSegment(sketch, "E41.8.4", {"start": v(-6.97, -13.52) * mm, "end": v(-7.53, -13.2) * mm});
            skLineSegment(sketch, "E41.9.0", {"start": v(2.3, -14.94) * mm, "end": v(1.66, -15.04) * mm});
            skLineSegment(sketch, "E41.9.1", {"start": v(1.66, -15.04) * mm, "end": v(1.02, -13.88) * mm});
            skLineSegment(sketch, "E41.9.2", {"start": v(1.02, -13.88) * mm, "end": v(-1.52, -13.88) * mm});
            skLineSegment(sketch, "E41.9.3", {"start": v(-1.52, -13.88) * mm, "end": v(-2.15, -15.04) * mm});
            skLineSegment(sketch, "E41.9.4", {"start": v(-2.15, -15.04) * mm, "end": v(-2.79, -14.94) * mm});
            skLineSegment(sketch, "E41.10.0", {"start": v(7.04, -13.2) * mm, "end": v(6.48, -13.52) * mm});
            skLineSegment(sketch, "E41.10.1", {"start": v(6.48, -13.52) * mm, "end": v(5.49, -12.65) * mm});
            skLineSegment(sketch, "E41.10.2", {"start": v(5.49, -12.65) * mm, "end": v(3.1, -13.52) * mm});
            skLineSegment(sketch, "E41.10.3", {"start": v(3.1, -13.52) * mm, "end": v(2.9, -14.82) * mm});
            skLineSegment(sketch, "E41.10.4", {"start": v(2.9, -14.82) * mm, "end": v(2.27, -14.94) * mm});
            skLineSegment(sketch, "E41.11.0", {"start": v(10.91, -9.95) * mm, "end": v(10.49, -10.44) * mm});
            skLineSegment(sketch, "E41.11.1", {"start": v(10.49, -10.44) * mm, "end": v(9.26, -9.96) * mm});
            skLineSegment(sketch, "E41.11.2", {"start": v(9.26, -9.96) * mm, "end": v(7.31, -11.6) * mm});
            skLineSegment(sketch, "E41.11.3", {"start": v(7.31, -11.6) * mm, "end": v(7.57, -12.89) * mm});
            skLineSegment(sketch, "E41.11.4", {"start": v(7.57, -12.89) * mm, "end": v(7.02, -13.22) * mm});
            skLineSegment(sketch, "E41.12.0", {"start": v(13.43, -5.57) * mm, "end": v(13.2, -6.17) * mm});
            skLineSegment(sketch, "E41.12.1", {"start": v(13.2, -6.17) * mm, "end": v(11.88, -6.15) * mm});
            skLineSegment(sketch, "E41.12.2", {"start": v(11.88, -6.15) * mm, "end": v(10.61, -8.35) * mm});
            skLineSegment(sketch, "E41.12.3", {"start": v(10.61, -8.35) * mm, "end": v(11.3, -9.47) * mm});
            skLineSegment(sketch, "E41.12.4", {"start": v(11.3, -9.47) * mm, "end": v(10.9, -9.97) * mm});
            skLineSegment(sketch, "E41.13.0", {"start": v(14.3, -0.6) * mm, "end": v(14.3, -1.24) * mm});
            skLineSegment(sketch, "E41.13.1", {"start": v(14.3, -1.24) * mm, "end": v(13.05, -1.66) * mm});
            skLineSegment(sketch, "E41.13.2", {"start": v(13.05, -1.66) * mm, "end": v(12.6, -4.16) * mm});
            skLineSegment(sketch, "E41.13.3", {"start": v(12.6, -4.16) * mm, "end": v(13.63, -5) * mm});
            skLineSegment(sketch, "E41.13.4", {"start": v(13.63, -5) * mm, "end": v(13.43, -5.6) * mm});
            skLineSegment(sketch, "E41.14.0", {"start": v(13.43, 4.38) * mm, "end": v(13.63, 3.77) * mm});
            skLineSegment(sketch, "E41.14.1", {"start": v(13.63, 3.77) * mm, "end": v(12.6, 2.95) * mm});
            skLineSegment(sketch, "E41.14.2", {"start": v(12.6, 2.95) * mm, "end": v(13.05, 0.45) * mm});
            skLineSegment(sketch, "E41.14.3", {"start": v(13.05, 0.45) * mm, "end": v(14.3, 0.02) * mm});
            skLineSegment(sketch, "E41.14.4", {"start": v(14.3, 0.02) * mm, "end": v(14.3, -0.62) * mm});
            skLineSegment(sketch, "E41.15.0", {"start": v(10.9, 8.76) * mm, "end": v(11.3, 8.26) * mm});
            skLineSegment(sketch, "E41.15.1", {"start": v(11.3, 8.26) * mm, "end": v(10.61, 7.13) * mm});
            skLineSegment(sketch, "E41.15.2", {"start": v(10.61, 7.13) * mm, "end": v(11.88, 4.93) * mm});
            skLineSegment(sketch, "E41.15.3", {"start": v(11.88, 4.93) * mm, "end": v(13.2, 4.96) * mm});
            skLineSegment(sketch, "E41.15.4", {"start": v(13.2, 4.96) * mm, "end": v(13.43, 4.36) * mm});
            skLineSegment(sketch, "E41.16.0", {"start": v(7.02, 12) * mm, "end": v(7.57, 11.67) * mm});
            skLineSegment(sketch, "E41.16.1", {"start": v(7.57, 11.67) * mm, "end": v(7.31, 10.38) * mm});
            skLineSegment(sketch, "E41.16.2", {"start": v(7.31, 10.38) * mm, "end": v(9.26, 8.74) * mm});
            skLineSegment(sketch, "E41.16.3", {"start": v(9.26, 8.74) * mm, "end": v(10.49, 9.22) * mm});
            skLineSegment(sketch, "E41.16.4", {"start": v(10.49, 9.22) * mm, "end": v(10.91, 8.74) * mm});
            skLineSegment(sketch, "E41.17.0", {"start": v(2.27, 13.73) * mm, "end": v(2.9, 13.6) * mm});
            skLineSegment(sketch, "E41.17.1", {"start": v(2.9, 13.6) * mm, "end": v(3.1, 12.3) * mm});
            skLineSegment(sketch, "E41.17.2", {"start": v(3.1, 12.3) * mm, "end": v(5.49, 11.43) * mm});
            skLineSegment(sketch, "E41.17.3", {"start": v(5.49, 11.43) * mm, "end": v(6.48, 12.3) * mm});
            skLineSegment(sketch, "E41.17.4", {"start": v(6.48, 12.3) * mm, "end": v(7.04, 11.99) * mm});
            skSolve(sketch);
        }
        {
            var Q0;
            Q0=makeQuery(id+"F8.imprint","IMPRINT",FACE,{"disambiguationData":[TD([[makeQuery(id+"F8.imprint","IMPRINT",EDGE,{"derivedFrom":sQuery(id+"F8.wireOp",EDGE,"E31")}),1.0]])]});
            var Q1;
            Q1=makeQuery(id+"F8.imprint","IMPRINT",FACE,{"disambiguationData":[TD([[makeQuery(id+"F8.imprint","IMPRINT",EDGE,{"derivedFrom":sQuery(id+"F8.wireOp",EDGE,"E28")}),-1.0]])]});
            var Q2;
            Q2=makeQuery(id+"F8.imprint","IMPRINT",FACE,{"disambiguationData":[TD([[makeQuery(id+"F8.imprint","IMPRINT",EDGE,{"derivedFrom":sQuery(id+"F8.wireOp",EDGE,"E28")}),1.0]])]});
            extrude(context, id + "F9", {"entities" : qUnion([Q0, Q1, Q2]), "endBound" : BoundingType.SYMMETRIC, "depth" : 14.3 * mm});
        }
        {
            var Q0;
            Q0=makeQuery(id+"F8.imprint","IMPRINT",FACE,{"disambiguationData":[TD([[makeQuery(id+"F8.imprint","IMPRINT",EDGE,{"derivedFrom":sQuery(id+"F8.wireOp",EDGE,"E31")}),1.0]])]});
            extrude(context, id + "F10", {"entities" : qUnion([Q0]), "operationType" : NewBodyOperationType.REMOVE, "endBound" : BoundingType.SYMMETRIC, "oppositeDirection" : true, "depth" : 10.92 * mm});
        }
        {
            var Q0;
            Q0=makeQuery(id+"F8.imprint","IMPRINT",FACE,{"disambiguationData":[TD([[makeQuery(id+"F8.imprint","IMPRINT",EDGE,{"derivedFrom":sQuery(id+"F8.wireOp",EDGE,"E28")}),1.0]])]});
            extrude(context, id + "F11", {"entities" : qUnion([Q0]), "operationType" : NewBodyOperationType.ADD, "depth" : 13.47 * mm});
        }
        {
            var Q0;
            Q0=qCreatedBy(makeId("Front.planeOp"),FACE);
            var sketch = newSketch(context, id + "F12", { "sketchPlane" : qUnion([Q0])});
            skCircle(sketch, "E42", {"center": v(-6.24, 6.7) * mm, "radius": 19.05 * mm});
            skCircle(sketch, "E43", {"center": v(-6.24, 6.7) * mm, "radius": 35.57 * mm, "construction": true});
            skCircle(sketch, "E44", {"center": v(-6.24, 6.7) * mm, "radius": 3.97 * mm});
            skPoint(sketch, "E45", {"position": v(-8.78, 42.2) * mm});
            skPoint(sketch, "E46", {"position": v(-3.7, 42.2) * mm});
            skPoint(sketch, "E47", {"position": v(-8.15, 42.23) * mm});
            skPoint(sketch, "E48", {"position": v(-4.34, 42.23) * mm});
            skLineSegment(sketch, "E49", {"start": v(-8.78, 42.2) * mm, "end": v(-8.15, 42.23) * mm});
            skLineSegment(sketch, "E50", {"start": v(-4.34, 42.23) * mm, "end": v(-3.7, 42.2) * mm});
            skLineSegment(sketch, "E51", {"start": v(-8.15, 42.23) * mm, "end": v(-7.51, 40.78) * mm});
            skLineSegment(sketch, "E52", {"start": v(-7.51, 40.78) * mm, "end": v(-4.97, 40.78) * mm});
            skLineSegment(sketch, "E53", {"start": v(-4.97, 40.78) * mm, "end": v(-4.34, 42.23) * mm});
            skLineSegment(sketch, "E54.1.0", {"start": v(-13.8, 41.47) * mm, "end": v(-13.18, 41.6) * mm});
            skLineSegment(sketch, "E54.1.1", {"start": v(-13.18, 41.6) * mm, "end": v(-12.35, 40.25) * mm});
            skLineSegment(sketch, "E54.1.2", {"start": v(-12.35, 40.25) * mm, "end": v(-9.83, 40.61) * mm});
            skLineSegment(sketch, "E54.1.3", {"start": v(-9.83, 40.61) * mm, "end": v(-9.41, 42.14) * mm});
            skLineSegment(sketch, "E54.1.4", {"start": v(-9.41, 42.14) * mm, "end": v(-8.78, 42.2) * mm});
            skLineSegment(sketch, "E54.2.0", {"start": v(-18.67, 40.04) * mm, "end": v(-18.08, 40.26) * mm});
            skLineSegment(sketch, "E54.2.1", {"start": v(-18.08, 40.26) * mm, "end": v(-17.06, 39.04) * mm});
            skLineSegment(sketch, "E54.2.2", {"start": v(-17.06, 39.04) * mm, "end": v(-14.62, 39.75) * mm});
            skLineSegment(sketch, "E54.2.3", {"start": v(-14.62, 39.75) * mm, "end": v(-14.42, 41.33) * mm});
            skLineSegment(sketch, "E54.2.4", {"start": v(-14.42, 41.33) * mm, "end": v(-13.8, 41.47) * mm});
            skLineSegment(sketch, "E54.3.0", {"start": v(-23.3, 37.93) * mm, "end": v(-22.73, 38.23) * mm});
            skLineSegment(sketch, "E54.3.1", {"start": v(-22.73, 38.23) * mm, "end": v(-21.55, 37.17) * mm});
            skLineSegment(sketch, "E54.3.2", {"start": v(-21.55, 37.17) * mm, "end": v(-19.24, 38.23) * mm});
            skLineSegment(sketch, "E54.3.3", {"start": v(-19.24, 38.23) * mm, "end": v(-19.26, 39.81) * mm});
            skLineSegment(sketch, "E54.3.4", {"start": v(-19.26, 39.81) * mm, "end": v(-18.67, 40.04) * mm});
            skLineSegment(sketch, "E54.4.0", {"start": v(-27.56, 35.19) * mm, "end": v(-27.05, 35.56) * mm});
            skLineSegment(sketch, "E54.4.1", {"start": v(-27.05, 35.56) * mm, "end": v(-25.73, 34.68) * mm});
            skLineSegment(sketch, "E54.4.2", {"start": v(-25.73, 34.68) * mm, "end": v(-23.6, 36.06) * mm});
            skLineSegment(sketch, "E54.4.3", {"start": v(-23.6, 36.06) * mm, "end": v(-23.84, 37.62) * mm});
            skLineSegment(sketch, "E54.4.4", {"start": v(-23.84, 37.62) * mm, "end": v(-23.29, 37.93) * mm});
            skLineSegment(sketch, "E54.5.0", {"start": v(-31.4, 31.86) * mm, "end": v(-30.94, 32.3) * mm});
            skLineSegment(sketch, "E54.5.1", {"start": v(-30.94, 32.3) * mm, "end": v(-29.5, 31.62) * mm});
            skLineSegment(sketch, "E54.5.2", {"start": v(-29.5, 31.62) * mm, "end": v(-27.59, 33.29) * mm});
            skLineSegment(sketch, "E54.5.3", {"start": v(-27.59, 33.29) * mm, "end": v(-28.06, 34.8) * mm});
            skLineSegment(sketch, "E54.5.4", {"start": v(-28.06, 34.8) * mm, "end": v(-27.56, 35.19) * mm});
            skLineSegment(sketch, "E54.6.0", {"start": v(-34.72, 28.03) * mm, "end": v(-34.33, 28.53) * mm});
            skLineSegment(sketch, "E54.6.1", {"start": v(-34.33, 28.53) * mm, "end": v(-32.82, 28.06) * mm});
            skLineSegment(sketch, "E54.6.2", {"start": v(-32.82, 28.06) * mm, "end": v(-31.15, 29.98) * mm});
            skLineSegment(sketch, "E54.6.3", {"start": v(-31.15, 29.98) * mm, "end": v(-31.84, 31.41) * mm});
            skLineSegment(sketch, "E54.6.4", {"start": v(-31.84, 31.41) * mm, "end": v(-31.4, 31.87) * mm});
            skLineSegment(sketch, "E54.7.0", {"start": v(-37.46, 23.76) * mm, "end": v(-37.15, 24.31) * mm});
            skLineSegment(sketch, "E54.7.1", {"start": v(-37.15, 24.31) * mm, "end": v(-35.59, 24.06) * mm});
            skLineSegment(sketch, "E54.7.2", {"start": v(-35.59, 24.06) * mm, "end": v(-34.21, 26.2) * mm});
            skLineSegment(sketch, "E54.7.3", {"start": v(-34.21, 26.2) * mm, "end": v(-35.1, 27.52) * mm});
            skLineSegment(sketch, "E54.7.4", {"start": v(-35.1, 27.52) * mm, "end": v(-34.72, 28.03) * mm});
            skLineSegment(sketch, "E54.8.0", {"start": v(-39.57, 19.14) * mm, "end": v(-39.34, 19.73) * mm});
            skLineSegment(sketch, "E54.8.1", {"start": v(-39.34, 19.73) * mm, "end": v(-37.76, 19.7) * mm});
            skLineSegment(sketch, "E54.8.2", {"start": v(-37.76, 19.7) * mm, "end": v(-36.7, 22.02) * mm});
            skLineSegment(sketch, "E54.8.3", {"start": v(-36.7, 22.02) * mm, "end": v(-37.76, 23.2) * mm});
            skLineSegment(sketch, "E54.8.4", {"start": v(-37.76, 23.2) * mm, "end": v(-37.46, 23.76) * mm});
            skLineSegment(sketch, "E54.9.0", {"start": v(-41, 14.27) * mm, "end": v(-40.86, 14.89) * mm});
            skLineSegment(sketch, "E54.9.1", {"start": v(-40.86, 14.89) * mm, "end": v(-39.29, 15.09) * mm});
            skLineSegment(sketch, "E54.9.2", {"start": v(-39.29, 15.09) * mm, "end": v(-38.57, 17.53) * mm});
            skLineSegment(sketch, "E54.9.3", {"start": v(-38.57, 17.53) * mm, "end": v(-39.79, 18.55) * mm});
            skLineSegment(sketch, "E54.9.4", {"start": v(-39.79, 18.55) * mm, "end": v(-39.57, 19.14) * mm});
            skLineSegment(sketch, "E54.10.0", {"start": v(-41.72, 9.25) * mm, "end": v(-41.67, 9.88) * mm});
            skLineSegment(sketch, "E54.10.1", {"start": v(-41.67, 9.88) * mm, "end": v(-40.14, 10.3) * mm});
            skLineSegment(sketch, "E54.10.2", {"start": v(-40.14, 10.3) * mm, "end": v(-39.78, 12.82) * mm});
            skLineSegment(sketch, "E54.10.3", {"start": v(-39.78, 12.82) * mm, "end": v(-41.13, 13.65) * mm});
            skLineSegment(sketch, "E54.10.4", {"start": v(-41.13, 13.65) * mm, "end": v(-41, 14.27) * mm});
            skLineSegment(sketch, "E54.11.0", {"start": v(-41.72, 4.17) * mm, "end": v(-41.76, 4.8) * mm});
            skLineSegment(sketch, "E54.11.1", {"start": v(-41.76, 4.8) * mm, "end": v(-40.3, 5.44) * mm});
            skLineSegment(sketch, "E54.11.2", {"start": v(-40.3, 5.44) * mm, "end": v(-40.3, 7.98) * mm});
            skLineSegment(sketch, "E54.11.3", {"start": v(-40.3, 7.98) * mm, "end": v(-41.76, 8.61) * mm});
            skLineSegment(sketch, "E54.11.4", {"start": v(-41.76, 8.61) * mm, "end": v(-41.72, 9.25) * mm});
            skLineSegment(sketch, "E54.12.0", {"start": v(-41, -0.85) * mm, "end": v(-41.13, -0.23) * mm});
            skLineSegment(sketch, "E54.12.1", {"start": v(-41.13, -0.23) * mm, "end": v(-39.78, 0.6) * mm});
            skLineSegment(sketch, "E54.12.2", {"start": v(-39.78, 0.6) * mm, "end": v(-40.14, 3.12) * mm});
            skLineSegment(sketch, "E54.12.3", {"start": v(-40.14, 3.12) * mm, "end": v(-41.67, 3.54) * mm});
            skLineSegment(sketch, "E54.12.4", {"start": v(-41.67, 3.54) * mm, "end": v(-41.72, 4.17) * mm});
            skLineSegment(sketch, "E54.13.0", {"start": v(-39.57, -5.72) * mm, "end": v(-39.79, -5.13) * mm});
            skLineSegment(sketch, "E54.13.1", {"start": v(-39.79, -5.13) * mm, "end": v(-38.57, -4.1) * mm});
            skLineSegment(sketch, "E54.13.2", {"start": v(-38.57, -4.1) * mm, "end": v(-39.29, -1.67) * mm});
            skLineSegment(sketch, "E54.13.3", {"start": v(-39.29, -1.67) * mm, "end": v(-40.86, -1.47) * mm});
            skLineSegment(sketch, "E54.13.4", {"start": v(-40.86, -1.47) * mm, "end": v(-41, -0.85) * mm});
            skLineSegment(sketch, "E54.14.0", {"start": v(-37.46, -10.34) * mm, "end": v(-37.76, -9.78) * mm});
            skLineSegment(sketch, "E54.14.1", {"start": v(-37.76, -9.78) * mm, "end": v(-36.7, -8.6) * mm});
            skLineSegment(sketch, "E54.14.2", {"start": v(-36.7, -8.6) * mm, "end": v(-37.76, -6.29) * mm});
            skLineSegment(sketch, "E54.14.3", {"start": v(-37.76, -6.29) * mm, "end": v(-39.34, -6.31) * mm});
            skLineSegment(sketch, "E54.14.4", {"start": v(-39.34, -6.31) * mm, "end": v(-39.57, -5.72) * mm});
            skLineSegment(sketch, "E54.15.0", {"start": v(-34.72, -14.6) * mm, "end": v(-35.1, -14.1) * mm});
            skLineSegment(sketch, "E54.15.1", {"start": v(-35.1, -14.1) * mm, "end": v(-34.21, -12.78) * mm});
            skLineSegment(sketch, "E54.15.2", {"start": v(-34.21, -12.78) * mm, "end": v(-35.59, -10.64) * mm});
            skLineSegment(sketch, "E54.15.3", {"start": v(-35.59, -10.64) * mm, "end": v(-37.15, -10.9) * mm});
            skLineSegment(sketch, "E54.15.4", {"start": v(-37.15, -10.9) * mm, "end": v(-37.46, -10.34) * mm});
            skLineSegment(sketch, "E54.16.0", {"start": v(-31.4, -18.45) * mm, "end": v(-31.84, -18) * mm});
            skLineSegment(sketch, "E54.16.1", {"start": v(-31.84, -18) * mm, "end": v(-31.15, -16.56) * mm});
            skLineSegment(sketch, "E54.16.2", {"start": v(-31.15, -16.56) * mm, "end": v(-32.82, -14.64) * mm});
            skLineSegment(sketch, "E54.16.3", {"start": v(-32.82, -14.64) * mm, "end": v(-34.33, -15.11) * mm});
            skLineSegment(sketch, "E54.16.4", {"start": v(-34.33, -15.11) * mm, "end": v(-34.72, -14.6) * mm});
            skLineSegment(sketch, "E54.17.0", {"start": v(-27.56, -21.77) * mm, "end": v(-28.06, -21.38) * mm});
            skLineSegment(sketch, "E54.17.1", {"start": v(-28.06, -21.38) * mm, "end": v(-27.59, -19.87) * mm});
            skLineSegment(sketch, "E54.17.2", {"start": v(-27.59, -19.87) * mm, "end": v(-29.5, -18.2) * mm});
            skLineSegment(sketch, "E54.17.3", {"start": v(-29.5, -18.2) * mm, "end": v(-30.94, -18.89) * mm});
            skLineSegment(sketch, "E54.17.4", {"start": v(-30.94, -18.89) * mm, "end": v(-31.4, -18.44) * mm});
            skLineSegment(sketch, "E54.18.0", {"start": v(-23.29, -24.51) * mm, "end": v(-23.84, -24.2) * mm});
            skLineSegment(sketch, "E54.18.1", {"start": v(-23.84, -24.2) * mm, "end": v(-23.6, -22.64) * mm});
            skLineSegment(sketch, "E54.18.2", {"start": v(-23.6, -22.64) * mm, "end": v(-25.73, -21.26) * mm});
            skLineSegment(sketch, "E54.18.3", {"start": v(-25.73, -21.26) * mm, "end": v(-27.05, -22.14) * mm});
            skLineSegment(sketch, "E54.18.4", {"start": v(-27.05, -22.14) * mm, "end": v(-27.56, -21.77) * mm});
            skLineSegment(sketch, "E54.19.0", {"start": v(-18.67, -26.62) * mm, "end": v(-19.26, -26.4) * mm});
            skLineSegment(sketch, "E54.19.1", {"start": v(-19.26, -26.4) * mm, "end": v(-19.24, -24.8) * mm});
            skLineSegment(sketch, "E54.19.2", {"start": v(-19.24, -24.8) * mm, "end": v(-21.55, -23.75) * mm});
            skLineSegment(sketch, "E54.19.3", {"start": v(-21.55, -23.75) * mm, "end": v(-22.73, -24.81) * mm});
            skLineSegment(sketch, "E54.19.4", {"start": v(-22.73, -24.81) * mm, "end": v(-23.3, -24.51) * mm});
            skLineSegment(sketch, "E54.20.0", {"start": v(-13.8, -28.05) * mm, "end": v(-14.42, -27.9) * mm});
            skLineSegment(sketch, "E54.20.1", {"start": v(-14.42, -27.9) * mm, "end": v(-14.62, -26.33) * mm});
            skLineSegment(sketch, "E54.20.2", {"start": v(-14.62, -26.33) * mm, "end": v(-17.06, -25.62) * mm});
            skLineSegment(sketch, "E54.20.3", {"start": v(-17.06, -25.62) * mm, "end": v(-18.08, -26.84) * mm});
            skLineSegment(sketch, "E54.20.4", {"start": v(-18.08, -26.84) * mm, "end": v(-18.67, -26.62) * mm});
            skLineSegment(sketch, "E54.21.0", {"start": v(-8.78, -28.77) * mm, "end": v(-9.41, -28.72) * mm});
            skLineSegment(sketch, "E54.21.1", {"start": v(-9.41, -28.72) * mm, "end": v(-9.83, -27.2) * mm});
            skLineSegment(sketch, "E54.21.2", {"start": v(-9.83, -27.2) * mm, "end": v(-12.35, -26.83) * mm});
            skLineSegment(sketch, "E54.21.3", {"start": v(-12.35, -26.83) * mm, "end": v(-13.18, -28.18) * mm});
            skLineSegment(sketch, "E54.21.4", {"start": v(-13.18, -28.18) * mm, "end": v(-13.8, -28.05) * mm});
            skLineSegment(sketch, "E54.22.0", {"start": v(-3.7, -28.77) * mm, "end": v(-4.34, -28.81) * mm});
            skLineSegment(sketch, "E54.22.1", {"start": v(-4.34, -28.81) * mm, "end": v(-4.97, -27.36) * mm});
            skLineSegment(sketch, "E54.22.2", {"start": v(-4.97, -27.36) * mm, "end": v(-7.51, -27.36) * mm});
            skLineSegment(sketch, "E54.22.3", {"start": v(-7.51, -27.36) * mm, "end": v(-8.15, -28.81) * mm});
            skLineSegment(sketch, "E54.22.4", {"start": v(-8.15, -28.81) * mm, "end": v(-8.78, -28.77) * mm});
            skLineSegment(sketch, "E54.23.0", {"start": v(1.32, -28.05) * mm, "end": v(0.7, -28.18) * mm});
            skLineSegment(sketch, "E54.23.1", {"start": v(0.7, -28.18) * mm, "end": v(-0.14, -26.83) * mm});
            skLineSegment(sketch, "E54.23.2", {"start": v(-0.14, -26.83) * mm, "end": v(-2.65, -27.2) * mm});
            skLineSegment(sketch, "E54.23.3", {"start": v(-2.65, -27.2) * mm, "end": v(-3.07, -28.72) * mm});
            skLineSegment(sketch, "E54.23.4", {"start": v(-3.07, -28.72) * mm, "end": v(-3.7, -28.77) * mm});
            skLineSegment(sketch, "E54.24.0", {"start": v(6.2, -26.62) * mm, "end": v(5.6, -26.84) * mm});
            skLineSegment(sketch, "E54.24.1", {"start": v(5.6, -26.84) * mm, "end": v(4.58, -25.62) * mm});
            skLineSegment(sketch, "E54.24.2", {"start": v(4.58, -25.62) * mm, "end": v(2.14, -26.33) * mm});
            skLineSegment(sketch, "E54.24.3", {"start": v(2.14, -26.33) * mm, "end": v(1.94, -27.9) * mm});
            skLineSegment(sketch, "E54.24.4", {"start": v(1.94, -27.9) * mm, "end": v(1.32, -28.05) * mm});
            skLineSegment(sketch, "E54.25.0", {"start": v(10.8, -24.51) * mm, "end": v(10.25, -24.81) * mm});
            skLineSegment(sketch, "E54.25.1", {"start": v(10.25, -24.81) * mm, "end": v(9.07, -23.75) * mm});
            skLineSegment(sketch, "E54.25.2", {"start": v(9.07, -23.75) * mm, "end": v(6.76, -24.8) * mm});
            skLineSegment(sketch, "E54.25.3", {"start": v(6.76, -24.8) * mm, "end": v(6.78, -26.4) * mm});
            skLineSegment(sketch, "E54.25.4", {"start": v(6.78, -26.4) * mm, "end": v(6.19, -26.62) * mm});
            skLineSegment(sketch, "E54.26.0", {"start": v(15.08, -21.77) * mm, "end": v(14.57, -22.14) * mm});
            skLineSegment(sketch, "E54.26.1", {"start": v(14.57, -22.14) * mm, "end": v(13.25, -21.26) * mm});
            skLineSegment(sketch, "E54.26.2", {"start": v(13.25, -21.26) * mm, "end": v(11.1, -22.64) * mm});
            skLineSegment(sketch, "E54.26.3", {"start": v(11.1, -22.64) * mm, "end": v(11.36, -24.2) * mm});
            skLineSegment(sketch, "E54.26.4", {"start": v(11.36, -24.2) * mm, "end": v(10.8, -24.51) * mm});
            skLineSegment(sketch, "E54.27.0", {"start": v(18.91, -18.44) * mm, "end": v(18.46, -18.89) * mm});
            skLineSegment(sketch, "E54.27.1", {"start": v(18.46, -18.89) * mm, "end": v(17.03, -18.2) * mm});
            skLineSegment(sketch, "E54.27.2", {"start": v(17.03, -18.2) * mm, "end": v(15.1, -19.87) * mm});
            skLineSegment(sketch, "E54.27.3", {"start": v(15.1, -19.87) * mm, "end": v(15.58, -21.38) * mm});
            skLineSegment(sketch, "E54.27.4", {"start": v(15.58, -21.38) * mm, "end": v(15.08, -21.77) * mm});
            skLineSegment(sketch, "E55.1.28.0", {"start": v(22.24, -14.6) * mm, "end": v(21.85, -15.11) * mm});
            skLineSegment(sketch, "E55.3.28.0", {"start": v(21.85, -15.11) * mm, "end": v(20.34, -14.64) * mm});
            skLineSegment(sketch, "E55.6.28.0", {"start": v(20.34, -14.64) * mm, "end": v(18.67, -16.56) * mm});
            skLineSegment(sketch, "E55.9.28.0", {"start": v(18.67, -16.56) * mm, "end": v(19.36, -18) * mm});
            skLineSegment(sketch, "E55.12.28.0", {"start": v(19.36, -18) * mm, "end": v(18.91, -18.45) * mm});
            skLineSegment(sketch, "E55.1.29.0", {"start": v(24.98, -10.34) * mm, "end": v(24.67, -10.9) * mm});
            skLineSegment(sketch, "E55.3.29.0", {"start": v(24.67, -10.9) * mm, "end": v(23.1, -10.64) * mm});
            skLineSegment(sketch, "E55.6.29.0", {"start": v(23.1, -10.64) * mm, "end": v(21.73, -12.78) * mm});
            skLineSegment(sketch, "E55.9.29.0", {"start": v(21.73, -12.78) * mm, "end": v(22.61, -14.1) * mm});
            skLineSegment(sketch, "E55.12.29.0", {"start": v(22.61, -14.1) * mm, "end": v(22.24, -14.6) * mm});
            skLineSegment(sketch, "E55.1.30.0", {"start": v(27.1, -5.72) * mm, "end": v(26.86, -6.31) * mm});
            skLineSegment(sketch, "E55.3.30.0", {"start": v(26.86, -6.31) * mm, "end": v(25.28, -6.29) * mm});
            skLineSegment(sketch, "E55.6.30.0", {"start": v(25.28, -6.29) * mm, "end": v(24.22, -8.6) * mm});
            skLineSegment(sketch, "E55.9.30.0", {"start": v(24.22, -8.6) * mm, "end": v(25.28, -9.78) * mm});
            skLineSegment(sketch, "E55.12.30.0", {"start": v(25.28, -9.78) * mm, "end": v(24.98, -10.34) * mm});
            skLineSegment(sketch, "E55.1.31.0", {"start": v(28.52, -0.85) * mm, "end": v(28.38, -1.47) * mm});
            skLineSegment(sketch, "E55.3.31.0", {"start": v(28.38, -1.47) * mm, "end": v(26.8, -1.67) * mm});
            skLineSegment(sketch, "E55.6.31.0", {"start": v(26.8, -1.67) * mm, "end": v(26.09, -4.1) * mm});
            skLineSegment(sketch, "E55.9.31.0", {"start": v(26.09, -4.1) * mm, "end": v(27.3, -5.13) * mm});
            skLineSegment(sketch, "E55.12.31.0", {"start": v(27.3, -5.13) * mm, "end": v(27.09, -5.72) * mm});
            skLineSegment(sketch, "E55.1.32.0", {"start": v(29.24, 4.17) * mm, "end": v(29.2, 3.54) * mm});
            skLineSegment(sketch, "E55.3.32.0", {"start": v(29.2, 3.54) * mm, "end": v(27.66, 3.12) * mm});
            skLineSegment(sketch, "E55.6.32.0", {"start": v(27.66, 3.12) * mm, "end": v(27.3, 0.6) * mm});
            skLineSegment(sketch, "E55.9.32.0", {"start": v(27.3, 0.6) * mm, "end": v(28.65, -0.23) * mm});
            skLineSegment(sketch, "E55.12.32.0", {"start": v(28.65, -0.23) * mm, "end": v(28.52, -0.85) * mm});
            skLineSegment(sketch, "E55.1.33.0", {"start": v(29.24, 9.25) * mm, "end": v(29.28, 8.61) * mm});
            skLineSegment(sketch, "E55.3.33.0", {"start": v(29.28, 8.61) * mm, "end": v(27.83, 7.98) * mm});
            skLineSegment(sketch, "E55.6.33.0", {"start": v(27.83, 7.98) * mm, "end": v(27.83, 5.44) * mm});
            skLineSegment(sketch, "E55.9.33.0", {"start": v(27.83, 5.44) * mm, "end": v(29.28, 4.8) * mm});
            skLineSegment(sketch, "E55.12.33.0", {"start": v(29.28, 4.8) * mm, "end": v(29.24, 4.17) * mm});
            skLineSegment(sketch, "E55.1.34.0", {"start": v(28.52, 14.27) * mm, "end": v(28.65, 13.65) * mm});
            skLineSegment(sketch, "E55.3.34.0", {"start": v(28.65, 13.65) * mm, "end": v(27.3, 12.82) * mm});
            skLineSegment(sketch, "E55.6.34.0", {"start": v(27.3, 12.82) * mm, "end": v(27.66, 10.3) * mm});
            skLineSegment(sketch, "E55.9.34.0", {"start": v(27.66, 10.3) * mm, "end": v(29.2, 9.88) * mm});
            skLineSegment(sketch, "E55.12.34.0", {"start": v(29.2, 9.88) * mm, "end": v(29.24, 9.25) * mm});
            skLineSegment(sketch, "E55.1.35.0", {"start": v(27.09, 19.14) * mm, "end": v(27.3, 18.55) * mm});
            skLineSegment(sketch, "E55.3.35.0", {"start": v(27.3, 18.55) * mm, "end": v(26.09, 17.53) * mm});
            skLineSegment(sketch, "E55.6.35.0", {"start": v(26.09, 17.53) * mm, "end": v(26.8, 15.09) * mm});
            skLineSegment(sketch, "E55.9.35.0", {"start": v(26.8, 15.09) * mm, "end": v(28.38, 14.89) * mm});
            skLineSegment(sketch, "E55.12.35.0", {"start": v(28.38, 14.89) * mm, "end": v(28.52, 14.27) * mm});
            skLineSegment(sketch, "E55.1.36.0", {"start": v(24.98, 23.76) * mm, "end": v(25.28, 23.2) * mm});
            skLineSegment(sketch, "E55.3.36.0", {"start": v(25.28, 23.2) * mm, "end": v(24.22, 22.02) * mm});
            skLineSegment(sketch, "E55.6.36.0", {"start": v(24.22, 22.02) * mm, "end": v(25.28, 19.7) * mm});
            skLineSegment(sketch, "E55.9.36.0", {"start": v(25.28, 19.7) * mm, "end": v(26.86, 19.73) * mm});
            skLineSegment(sketch, "E55.12.36.0", {"start": v(26.86, 19.73) * mm, "end": v(27.1, 19.14) * mm});
            skLineSegment(sketch, "E55.1.37.0", {"start": v(22.24, 28.03) * mm, "end": v(22.61, 27.52) * mm});
            skLineSegment(sketch, "E55.3.37.0", {"start": v(22.61, 27.52) * mm, "end": v(21.73, 26.2) * mm});
            skLineSegment(sketch, "E55.6.37.0", {"start": v(21.73, 26.2) * mm, "end": v(23.1, 24.06) * mm});
            skLineSegment(sketch, "E55.9.37.0", {"start": v(23.1, 24.06) * mm, "end": v(24.67, 24.31) * mm});
            skLineSegment(sketch, "E55.12.37.0", {"start": v(24.67, 24.31) * mm, "end": v(24.98, 23.76) * mm});
            skLineSegment(sketch, "E55.1.38.0", {"start": v(18.91, 31.87) * mm, "end": v(19.36, 31.41) * mm});
            skLineSegment(sketch, "E55.3.38.0", {"start": v(19.36, 31.41) * mm, "end": v(18.67, 29.98) * mm});
            skLineSegment(sketch, "E55.6.38.0", {"start": v(18.67, 29.98) * mm, "end": v(20.34, 28.06) * mm});
            skLineSegment(sketch, "E55.9.38.0", {"start": v(20.34, 28.06) * mm, "end": v(21.85, 28.53) * mm});
            skLineSegment(sketch, "E55.12.38.0", {"start": v(21.85, 28.53) * mm, "end": v(22.24, 28.03) * mm});
            skLineSegment(sketch, "E55.1.39.0", {"start": v(15.08, 35.19) * mm, "end": v(15.58, 34.8) * mm});
            skLineSegment(sketch, "E55.3.39.0", {"start": v(15.58, 34.8) * mm, "end": v(15.1, 33.29) * mm});
            skLineSegment(sketch, "E55.6.39.0", {"start": v(15.1, 33.29) * mm, "end": v(17.03, 31.62) * mm});
            skLineSegment(sketch, "E55.9.39.0", {"start": v(17.03, 31.62) * mm, "end": v(18.46, 32.3) * mm});
            skLineSegment(sketch, "E55.12.39.0", {"start": v(18.46, 32.3) * mm, "end": v(18.91, 31.86) * mm});
            skLineSegment(sketch, "E55.1.40.0", {"start": v(10.8, 37.93) * mm, "end": v(11.36, 37.62) * mm});
            skLineSegment(sketch, "E55.3.40.0", {"start": v(11.36, 37.62) * mm, "end": v(11.1, 36.06) * mm});
            skLineSegment(sketch, "E55.6.40.0", {"start": v(11.1, 36.06) * mm, "end": v(13.25, 34.68) * mm});
            skLineSegment(sketch, "E55.9.40.0", {"start": v(13.25, 34.68) * mm, "end": v(14.57, 35.56) * mm});
            skLineSegment(sketch, "E55.12.40.0", {"start": v(14.57, 35.56) * mm, "end": v(15.08, 35.19) * mm});
            skLineSegment(sketch, "E55.1.41.0", {"start": v(6.19, 40.04) * mm, "end": v(6.78, 39.81) * mm});
            skLineSegment(sketch, "E55.3.41.0", {"start": v(6.78, 39.81) * mm, "end": v(6.76, 38.23) * mm});
            skLineSegment(sketch, "E55.6.41.0", {"start": v(6.76, 38.23) * mm, "end": v(9.07, 37.17) * mm});
            skLineSegment(sketch, "E55.9.41.0", {"start": v(9.07, 37.17) * mm, "end": v(10.25, 38.23) * mm});
            skLineSegment(sketch, "E55.12.41.0", {"start": v(10.25, 38.23) * mm, "end": v(10.8, 37.93) * mm});
            skLineSegment(sketch, "E55.1.42.0", {"start": v(1.32, 41.47) * mm, "end": v(1.94, 41.33) * mm});
            skLineSegment(sketch, "E55.3.42.0", {"start": v(1.94, 41.33) * mm, "end": v(2.14, 39.75) * mm});
            skLineSegment(sketch, "E55.6.42.0", {"start": v(2.14, 39.75) * mm, "end": v(4.58, 39.04) * mm});
            skLineSegment(sketch, "E55.9.42.0", {"start": v(4.58, 39.04) * mm, "end": v(5.6, 40.26) * mm});
            skLineSegment(sketch, "E55.12.42.0", {"start": v(5.6, 40.26) * mm, "end": v(6.2, 40.04) * mm});
            skLineSegment(sketch, "E55.1.43.0", {"start": v(-3.7, 42.2) * mm, "end": v(-3.07, 42.14) * mm});
            skLineSegment(sketch, "E55.3.43.0", {"start": v(-3.07, 42.14) * mm, "end": v(-2.65, 40.61) * mm});
            skLineSegment(sketch, "E55.6.43.0", {"start": v(-2.65, 40.61) * mm, "end": v(-0.14, 40.25) * mm});
            skLineSegment(sketch, "E55.9.43.0", {"start": v(-0.14, 40.25) * mm, "end": v(0.7, 41.6) * mm});
            skLineSegment(sketch, "E55.12.43.0", {"start": v(0.7, 41.6) * mm, "end": v(1.32, 41.47) * mm});
            skSolve(sketch);
        }
        {
            var Q0;
            Q0=makeQuery(id+"F12.imprint","IMPRINT",FACE,{"disambiguationData":[TD([[makeQuery(id+"F12.imprint","IMPRINT",EDGE,{"derivedFrom":sQuery(id+"F12.wireOp",EDGE,"E42")}),-1.0]])]});
            var Q1;
            Q1=makeQuery(id+"F12.imprint","IMPRINT",FACE,{"disambiguationData":[TD([[makeQuery(id+"F12.imprint","IMPRINT",EDGE,{"derivedFrom":sQuery(id+"F12.wireOp",EDGE,"E42")}),1.0]])]});
            extrude(context, id + "F13", {"entities" : qUnion([Q0, Q1]), "endBound" : BoundingType.SYMMETRIC, "depth" : 14.3 * mm});
        }
        {
            var Q0;
            Q0=makeQuery(id+"F12.imprint","IMPRINT",FACE,{"disambiguationData":[TD([[makeQuery(id+"F12.imprint","IMPRINT",EDGE,{"derivedFrom":sQuery(id+"F12.wireOp",EDGE,"E42")}),1.0]])]});
            extrude(context, id + "F14", {"entities" : qUnion([Q0]), "operationType" : NewBodyOperationType.ADD, "depth" : 18.25 * mm});
        }
        {
            var Q0;
            Q0=qCreatedBy(makeId("Front.planeOp"),FACE);
            var sketch = newSketch(context, id + "F15", { "sketchPlane" : qUnion([Q0])});
            skCircle(sketch, "E56", {"center": v(0.03, -0.53) * mm, "radius": 7.94 * mm});
            skCircle(sketch, "E57", {"center": v(0.03, -0.53) * mm, "radius": 12.13 * mm, "construction": true});
            skCircle(sketch, "E58", {"center": v(0.03, -0.53) * mm, "radius": 3.97 * mm});
            skCircle(sketch, "E59", {"center": v(0.03, -0.53) * mm, "radius": 15.09 * mm});
            skPoint(sketch, "E60", {"position": v(-2.5, 11.33) * mm});
            skPoint(sketch, "E61", {"position": v(2.57, 11.33) * mm});
            skPoint(sketch, "E62", {"position": v(-1.87, 11.45) * mm});
            skPoint(sketch, "E63", {"position": v(1.94, 11.45) * mm});
            skLineSegment(sketch, "E64", {"start": v(-2.5, 11.33) * mm, "end": v(-1.87, 11.45) * mm});
            skLineSegment(sketch, "E65", {"start": v(1.94, 11.45) * mm, "end": v(2.57, 11.33) * mm});
            skLineSegment(sketch, "E66", {"start": v(-1.87, 11.45) * mm, "end": v(-1.24, 10.37) * mm});
            skLineSegment(sketch, "E67", {"start": v(-1.24, 10.37) * mm, "end": v(1.3, 10.37) * mm});
            skLineSegment(sketch, "E68", {"start": v(1.3, 10.37) * mm, "end": v(1.94, 11.45) * mm});
            skLineSegment(sketch, "E69.1.0", {"start": v(-7.11, 9.27) * mm, "end": v(-6.58, 9.64) * mm});
            skLineSegment(sketch, "E69.1.1", {"start": v(-6.58, 9.64) * mm, "end": v(-5.56, 8.91) * mm});
            skLineSegment(sketch, "E69.1.2", {"start": v(-5.56, 8.91) * mm, "end": v(-3.24, 9.94) * mm});
            skLineSegment(sketch, "E69.1.3", {"start": v(-3.24, 9.94) * mm, "end": v(-3.1, 11.19) * mm});
            skLineSegment(sketch, "E69.1.4", {"start": v(-3.1, 11.19) * mm, "end": v(-2.47, 11.34) * mm});
            skLineSegment(sketch, "E69.2.0", {"start": v(-10.48, 5.52) * mm, "end": v(-10.14, 6.07) * mm});
            skLineSegment(sketch, "E69.2.1", {"start": v(-10.14, 6.07) * mm, "end": v(-8.92, 5.82) * mm});
            skLineSegment(sketch, "E69.2.2", {"start": v(-8.92, 5.82) * mm, "end": v(-7.22, 7.7) * mm});
            skLineSegment(sketch, "E69.2.3", {"start": v(-7.22, 7.7) * mm, "end": v(-7.6, 8.9) * mm});
            skLineSegment(sketch, "E69.2.4", {"start": v(-7.6, 8.9) * mm, "end": v(-7.08, 9.3) * mm});
            skLineSegment(sketch, "E69.3.0", {"start": v(-12.03, 0.72) * mm, "end": v(-11.95, 1.36) * mm});
            skLineSegment(sketch, "E69.3.1", {"start": v(-11.95, 1.36) * mm, "end": v(-10.73, 1.63) * mm});
            skLineSegment(sketch, "E69.3.2", {"start": v(-10.73, 1.63) * mm, "end": v(-9.95, 4.05) * mm});
            skLineSegment(sketch, "E69.3.3", {"start": v(-9.95, 4.05) * mm, "end": v(-10.77, 4.98) * mm});
            skLineSegment(sketch, "E69.3.4", {"start": v(-10.77, 4.98) * mm, "end": v(-10.46, 5.55) * mm});
            skLineSegment(sketch, "E69.4.0", {"start": v(-11.5, -4.3) * mm, "end": v(-11.68, -3.68) * mm});
            skLineSegment(sketch, "E69.4.1", {"start": v(-11.68, -3.68) * mm, "end": v(-10.68, -2.93) * mm});
            skLineSegment(sketch, "E69.4.2", {"start": v(-10.68, -2.93) * mm, "end": v(-10.94, -0.4) * mm});
            skLineSegment(sketch, "E69.4.3", {"start": v(-10.94, -0.4) * mm, "end": v(-12.08, 0.11) * mm});
            skLineSegment(sketch, "E69.4.4", {"start": v(-12.08, 0.11) * mm, "end": v(-12.03, 0.75) * mm});
            skLineSegment(sketch, "E69.5.0", {"start": v(-8.97, -8.66) * mm, "end": v(-9.39, -8.17) * mm});
            skLineSegment(sketch, "E69.5.1", {"start": v(-9.39, -8.17) * mm, "end": v(-8.78, -7.08) * mm});
            skLineSegment(sketch, "E69.5.2", {"start": v(-8.78, -7.08) * mm, "end": v(-10.05, -4.88) * mm});
            skLineSegment(sketch, "E69.5.3", {"start": v(-10.05, -4.88) * mm, "end": v(-11.3, -4.87) * mm});
            skLineSegment(sketch, "E69.5.4", {"start": v(-11.3, -4.87) * mm, "end": v(-11.5, -4.26) * mm});
            skLineSegment(sketch, "E69.6.0", {"start": v(-4.88, -11.62) * mm, "end": v(-5.47, -11.34) * mm});
            skLineSegment(sketch, "E69.6.1", {"start": v(-5.47, -11.34) * mm, "end": v(-5.35, -10.1) * mm});
            skLineSegment(sketch, "E69.6.2", {"start": v(-5.35, -10.1) * mm, "end": v(-7.4, -8.6) * mm});
            skLineSegment(sketch, "E69.6.3", {"start": v(-7.4, -8.6) * mm, "end": v(-8.55, -9.1) * mm});
            skLineSegment(sketch, "E69.6.4", {"start": v(-8.55, -9.1) * mm, "end": v(-9, -8.63) * mm});
            skLineSegment(sketch, "E69.7.0", {"start": v(0.05, -12.66) * mm, "end": v(-0.6, -12.64) * mm});
            skLineSegment(sketch, "E69.7.1", {"start": v(-0.6, -12.64) * mm, "end": v(-1, -11.46) * mm});
            skLineSegment(sketch, "E69.7.2", {"start": v(-1, -11.46) * mm, "end": v(-3.48, -10.93) * mm});
            skLineSegment(sketch, "E69.7.3", {"start": v(-3.48, -10.93) * mm, "end": v(-4.32, -11.85) * mm});
            skLineSegment(sketch, "E69.7.4", {"start": v(-4.32, -11.85) * mm, "end": v(-4.92, -11.6) * mm});
            skLineSegment(sketch, "E69.8.0", {"start": v(4.98, -11.6) * mm, "end": v(4.38, -11.85) * mm});
            skLineSegment(sketch, "E69.8.1", {"start": v(4.38, -11.85) * mm, "end": v(3.54, -10.93) * mm});
            skLineSegment(sketch, "E69.8.2", {"start": v(3.54, -10.93) * mm, "end": v(1.06, -11.46) * mm});
            skLineSegment(sketch, "E69.8.3", {"start": v(1.06, -11.46) * mm, "end": v(0.66, -12.64) * mm});
            skLineSegment(sketch, "E69.8.4", {"start": v(0.66, -12.64) * mm, "end": v(0.01, -12.66) * mm});
            skLineSegment(sketch, "E69.9.0", {"start": v(9.06, -8.63) * mm, "end": v(8.61, -9.1) * mm});
            skLineSegment(sketch, "E69.9.1", {"start": v(8.61, -9.1) * mm, "end": v(7.47, -8.6) * mm});
            skLineSegment(sketch, "E69.9.2", {"start": v(7.47, -8.6) * mm, "end": v(5.41, -10.1) * mm});
            skLineSegment(sketch, "E69.9.3", {"start": v(5.41, -10.1) * mm, "end": v(5.53, -11.34) * mm});
            skLineSegment(sketch, "E69.9.4", {"start": v(5.53, -11.34) * mm, "end": v(4.95, -11.62) * mm});
            skLineSegment(sketch, "E69.10.0", {"start": v(11.57, -4.26) * mm, "end": v(11.36, -4.87) * mm});
            skLineSegment(sketch, "E69.10.1", {"start": v(11.36, -4.87) * mm, "end": v(10.1, -4.88) * mm});
            skLineSegment(sketch, "E69.10.2", {"start": v(10.1, -4.88) * mm, "end": v(8.84, -7.08) * mm});
            skLineSegment(sketch, "E69.10.3", {"start": v(8.84, -7.08) * mm, "end": v(9.45, -8.17) * mm});
            skLineSegment(sketch, "E69.10.4", {"start": v(9.45, -8.17) * mm, "end": v(9.03, -8.66) * mm});
            skLineSegment(sketch, "E69.11.0", {"start": v(12.1, 0.75) * mm, "end": v(12.14, 0.11) * mm});
            skLineSegment(sketch, "E69.11.1", {"start": v(12.14, 0.11) * mm, "end": v(11, -0.4) * mm});
            skLineSegment(sketch, "E69.11.2", {"start": v(11, -0.4) * mm, "end": v(10.74, -2.93) * mm});
            skLineSegment(sketch, "E69.11.3", {"start": v(10.74, -2.93) * mm, "end": v(11.74, -3.68) * mm});
            skLineSegment(sketch, "E69.11.4", {"start": v(11.74, -3.68) * mm, "end": v(11.56, -4.3) * mm});
            skLineSegment(sketch, "E69.12.0", {"start": v(10.53, 5.55) * mm, "end": v(10.83, 4.98) * mm});
            skLineSegment(sketch, "E69.12.1", {"start": v(10.83, 4.98) * mm, "end": v(10, 4.05) * mm});
            skLineSegment(sketch, "E69.12.2", {"start": v(10, 4.05) * mm, "end": v(10.8, 1.63) * mm});
            skLineSegment(sketch, "E69.12.3", {"start": v(10.8, 1.63) * mm, "end": v(12.01, 1.36) * mm});
            skLineSegment(sketch, "E69.12.4", {"start": v(12.01, 1.36) * mm, "end": v(12.1, 0.72) * mm});
            skLineSegment(sketch, "E69.13.0", {"start": v(7.14, 9.3) * mm, "end": v(7.66, 8.9) * mm});
            skLineSegment(sketch, "E69.13.1", {"start": v(7.66, 8.9) * mm, "end": v(7.28, 7.7) * mm});
            skLineSegment(sketch, "E69.13.2", {"start": v(7.28, 7.7) * mm, "end": v(8.98, 5.82) * mm});
            skLineSegment(sketch, "E69.13.3", {"start": v(8.98, 5.82) * mm, "end": v(10.2, 6.07) * mm});
            skLineSegment(sketch, "E69.13.4", {"start": v(10.2, 6.07) * mm, "end": v(10.54, 5.52) * mm});
            skLineSegment(sketch, "E70.1.14.0", {"start": v(2.53, 11.34) * mm, "end": v(3.16, 11.19) * mm});
            skLineSegment(sketch, "E70.3.14.0", {"start": v(3.16, 11.19) * mm, "end": v(3.3, 9.94) * mm});
            skLineSegment(sketch, "E70.6.14.0", {"start": v(3.3, 9.94) * mm, "end": v(5.63, 8.91) * mm});
            skLineSegment(sketch, "E70.9.14.0", {"start": v(5.63, 8.91) * mm, "end": v(6.64, 9.64) * mm});
            skLineSegment(sketch, "E70.12.14.0", {"start": v(6.64, 9.64) * mm, "end": v(7.18, 9.27) * mm});
            skSolve(sketch);
        }
        {
            var Q0;
            Q0=makeQuery(id+"F15.imprint","IMPRINT",FACE,{"disambiguationData":[TD([[makeQuery(id+"F15.imprint","IMPRINT",EDGE,{"derivedFrom":sQuery(id+"F15.wireOp",EDGE,"E59")}),1.0]])]});
            var Q1;
            Q1=makeQuery(id+"F15.imprint","IMPRINT",FACE,{"disambiguationData":[TD([[makeQuery(id+"F15.imprint","IMPRINT",EDGE,{"derivedFrom":sQuery(id+"F15.wireOp",EDGE,"E56")}),1.0]])]});
            var Q2;
            Q2=makeQuery(id+"F15.imprint","IMPRINT",FACE,{"disambiguationData":[TD([[makeQuery(id+"F15.imprint","IMPRINT",EDGE,{"derivedFrom":sQuery(id+"F15.wireOp",EDGE,"E56")}),-1.0]])]});
            extrude(context, id + "F16", {"entities" : qUnion([Q0, Q1, Q2]), "endBound" : BoundingType.SYMMETRIC, "depth" : 14.3 * mm});
        }
        {
            var Q0;
            Q0=makeQuery(id+"F15.imprint","IMPRINT",FACE,{"disambiguationData":[TD([[makeQuery(id+"F15.imprint","IMPRINT",EDGE,{"derivedFrom":sQuery(id+"F15.wireOp",EDGE,"E59")}),1.0]])]});
            extrude(context, id + "F17", {"entities" : qUnion([Q0]), "operationType" : NewBodyOperationType.REMOVE, "endBound" : BoundingType.SYMMETRIC, "oppositeDirection" : true, "depth" : 10.92 * mm});
        }
        {
            var Q0;
            Q0=makeQuery(id+"F15.imprint","IMPRINT",FACE,{"disambiguationData":[TD([[makeQuery(id+"F15.imprint","IMPRINT",EDGE,{"derivedFrom":sQuery(id+"F15.wireOp",EDGE,"E56")}),1.0]])]});
            extrude(context, id + "F18", {"entities" : qUnion([Q0]), "operationType" : NewBodyOperationType.ADD, "depth" : 13.47 * mm});
        }
        {
            var Q0;
            Q0=qCreatedBy(makeId("Front.planeOp"),FACE);
            var sketch = newSketch(context, id + "F19", { "sketchPlane" : qUnion([Q0])});
            skCircle(sketch, "E71", {"center": v(-0.05, -0.52) * mm, "radius": 5.55 * mm});
            skCircle(sketch, "E72", {"center": v(-0.05, -0.52) * mm, "radius": 8.09 * mm, "construction": true});
            skCircle(sketch, "E73", {"center": v(-0.05, -0.52) * mm, "radius": 2.5 * mm});
            skCircle(sketch, "E74", {"center": v(-0.05, -0.52) * mm, "radius": 11.11 * mm});
            skPoint(sketch, "E75", {"position": v(-2.6, 7.17) * mm});
            skPoint(sketch, "E76", {"position": v(2.49, 7.17) * mm});
            skPoint(sketch, "E77", {"position": v(-1.96, 7.35) * mm});
            skPoint(sketch, "E78", {"position": v(1.85, 7.35) * mm});
            skLineSegment(sketch, "E79", {"start": v(-2.6, 7.17) * mm, "end": v(-1.96, 7.35) * mm});
            skLineSegment(sketch, "E80", {"start": v(1.85, 7.35) * mm, "end": v(2.49, 7.17) * mm});
            skLineSegment(sketch, "E81", {"start": v(-1.96, 7.35) * mm, "end": v(-1.32, 6.47) * mm});
            skLineSegment(sketch, "E82", {"start": v(-1.32, 6.47) * mm, "end": v(1.22, 6.47) * mm});
            skLineSegment(sketch, "E83", {"start": v(1.22, 6.47) * mm, "end": v(1.85, 7.35) * mm});
            skLineSegment(sketch, "E84.1.0", {"start": v(-6.62, 4.2) * mm, "end": v(-6.21, 4.73) * mm});
            skLineSegment(sketch, "E84.1.1", {"start": v(-6.21, 4.73) * mm, "end": v(-5.19, 4.4) * mm});
            skLineSegment(sketch, "E84.1.2", {"start": v(-5.19, 4.4) * mm, "end": v(-3.13, 5.88) * mm});
            skLineSegment(sketch, "E84.1.3", {"start": v(-3.13, 5.88) * mm, "end": v(-3.13, 6.97) * mm});
            skLineSegment(sketch, "E84.1.4", {"start": v(-3.13, 6.97) * mm, "end": v(-2.51, 7.2) * mm});
            skLineSegment(sketch, "E84.2.0", {"start": v(-8.14, -0.56) * mm, "end": v(-8.12, 0.1) * mm});
            skLineSegment(sketch, "E84.2.1", {"start": v(-8.12, 0.1) * mm, "end": v(-7.09, 0.44) * mm});
            skLineSegment(sketch, "E84.2.2", {"start": v(-7.09, 0.44) * mm, "end": v(-6.3, 2.85) * mm});
            skLineSegment(sketch, "E84.2.3", {"start": v(-6.3, 2.85) * mm, "end": v(-6.94, 3.73) * mm});
            skLineSegment(sketch, "E84.2.4", {"start": v(-6.94, 3.73) * mm, "end": v(-6.57, 4.27) * mm});
            skLineSegment(sketch, "E84.3.0", {"start": v(-6.57, -5.3) * mm, "end": v(-6.94, -4.76) * mm});
            skLineSegment(sketch, "E84.3.1", {"start": v(-6.94, -4.76) * mm, "end": v(-6.3, -3.88) * mm});
            skLineSegment(sketch, "E84.3.2", {"start": v(-6.3, -3.88) * mm, "end": v(-7.09, -1.47) * mm});
            skLineSegment(sketch, "E84.3.3", {"start": v(-7.09, -1.47) * mm, "end": v(-8.12, -1.13) * mm});
            skLineSegment(sketch, "E84.3.4", {"start": v(-8.12, -1.13) * mm, "end": v(-8.14, -0.47) * mm});
            skLineSegment(sketch, "E84.4.0", {"start": v(-2.51, -8.22) * mm, "end": v(-3.13, -8) * mm});
            skLineSegment(sketch, "E84.4.1", {"start": v(-3.13, -8) * mm, "end": v(-3.13, -6.91) * mm});
            skLineSegment(sketch, "E84.4.2", {"start": v(-3.13, -6.91) * mm, "end": v(-5.19, -5.42) * mm});
            skLineSegment(sketch, "E84.4.3", {"start": v(-5.19, -5.42) * mm, "end": v(-6.21, -5.76) * mm});
            skLineSegment(sketch, "E84.4.4", {"start": v(-6.21, -5.76) * mm, "end": v(-6.62, -5.24) * mm});
            skLineSegment(sketch, "E84.5.0", {"start": v(2.49, -8.2) * mm, "end": v(1.85, -8.38) * mm});
            skLineSegment(sketch, "E84.5.1", {"start": v(1.85, -8.38) * mm, "end": v(1.22, -7.5) * mm});
            skLineSegment(sketch, "E84.5.2", {"start": v(1.22, -7.5) * mm, "end": v(-1.32, -7.5) * mm});
            skLineSegment(sketch, "E84.5.3", {"start": v(-1.32, -7.5) * mm, "end": v(-1.96, -8.38) * mm});
            skLineSegment(sketch, "E84.5.4", {"start": v(-1.96, -8.38) * mm, "end": v(-2.6, -8.2) * mm});
            skLineSegment(sketch, "E84.6.0", {"start": v(6.52, -5.24) * mm, "end": v(6.11, -5.76) * mm});
            skLineSegment(sketch, "E84.6.1", {"start": v(6.11, -5.76) * mm, "end": v(5.08, -5.42) * mm});
            skLineSegment(sketch, "E84.6.2", {"start": v(5.08, -5.42) * mm, "end": v(3.03, -6.91) * mm});
            skLineSegment(sketch, "E84.6.3", {"start": v(3.03, -6.91) * mm, "end": v(3.03, -8) * mm});
            skLineSegment(sketch, "E84.6.4", {"start": v(3.03, -8) * mm, "end": v(2.4, -8.22) * mm});
            skLineSegment(sketch, "E84.7.0", {"start": v(8.04, -0.47) * mm, "end": v(8.01, -1.13) * mm});
            skLineSegment(sketch, "E84.7.1", {"start": v(8.01, -1.13) * mm, "end": v(6.99, -1.47) * mm});
            skLineSegment(sketch, "E84.7.2", {"start": v(6.99, -1.47) * mm, "end": v(6.2, -3.88) * mm});
            skLineSegment(sketch, "E84.7.3", {"start": v(6.2, -3.88) * mm, "end": v(6.84, -4.76) * mm});
            skLineSegment(sketch, "E84.7.4", {"start": v(6.84, -4.76) * mm, "end": v(6.47, -5.3) * mm});
            skLineSegment(sketch, "E84.8.0", {"start": v(6.47, 4.27) * mm, "end": v(6.84, 3.73) * mm});
            skLineSegment(sketch, "E84.8.1", {"start": v(6.84, 3.73) * mm, "end": v(6.2, 2.85) * mm});
            skLineSegment(sketch, "E84.8.2", {"start": v(6.2, 2.85) * mm, "end": v(6.99, 0.44) * mm});
            skLineSegment(sketch, "E84.8.3", {"start": v(6.99, 0.44) * mm, "end": v(8.01, 0.1) * mm});
            skLineSegment(sketch, "E84.8.4", {"start": v(8.01, 0.1) * mm, "end": v(8.04, -0.56) * mm});
            skLineSegment(sketch, "E84.9.0", {"start": v(2.4, 7.2) * mm, "end": v(3.03, 6.97) * mm});
            skLineSegment(sketch, "E84.9.1", {"start": v(3.03, 6.97) * mm, "end": v(3.03, 5.88) * mm});
            skLineSegment(sketch, "E84.9.2", {"start": v(3.03, 5.88) * mm, "end": v(5.08, 4.4) * mm});
            skLineSegment(sketch, "E84.9.3", {"start": v(5.08, 4.4) * mm, "end": v(6.11, 4.73) * mm});
            skLineSegment(sketch, "E84.9.4", {"start": v(6.11, 4.73) * mm, "end": v(6.52, 4.2) * mm});
            skSolve(sketch);
        }
        {
            var Q0;
            Q0=makeQuery(id+"F19.imprint","IMPRINT",FACE,{"disambiguationData":[TD([[makeQuery(id+"F19.imprint","IMPRINT",EDGE,{"derivedFrom":sQuery(id+"F19.wireOp",EDGE,"E71")}),-1.0]])]});
            var Q1;
            Q1=makeQuery(id+"F19.imprint","IMPRINT",FACE,{"disambiguationData":[TD([[makeQuery(id+"F19.imprint","IMPRINT",EDGE,{"derivedFrom":sQuery(id+"F19.wireOp",EDGE,"E71")}),1.0]])]});
            var Q2;
            Q2=makeQuery(id+"F19.imprint","IMPRINT",FACE,{"disambiguationData":[TD([[makeQuery(id+"F19.imprint","IMPRINT",EDGE,{"derivedFrom":sQuery(id+"F19.wireOp",EDGE,"E74")}),1.0]])]});
            extrude(context, id + "F20", {"entities" : qUnion([Q0, Q1, Q2]), "endBound" : BoundingType.SYMMETRIC, "depth" : 14.3 * mm});
        }
        {
            var Q0;
            Q0=makeQuery(id+"F19.imprint","IMPRINT",FACE,{"disambiguationData":[TD([[makeQuery(id+"F19.imprint","IMPRINT",EDGE,{"derivedFrom":sQuery(id+"F19.wireOp",EDGE,"E74")}),1.0]])]});
            extrude(context, id + "F21", {"entities" : qUnion([Q0]), "operationType" : NewBodyOperationType.REMOVE, "endBound" : BoundingType.SYMMETRIC, "oppositeDirection" : true, "depth" : 10.92 * mm});
        }
        {
            var Q0;
            Q0=makeQuery(id+"F19.imprint","IMPRINT",FACE,{"disambiguationData":[TD([[makeQuery(id+"F19.imprint","IMPRINT",EDGE,{"derivedFrom":sQuery(id+"F19.wireOp",EDGE,"E71")}),1.0]])]});
            extrude(context, id + "F22", {"entities" : qUnion([Q0]), "operationType" : NewBodyOperationType.ADD, "depth" : 13.47 * mm});
        }
    });
